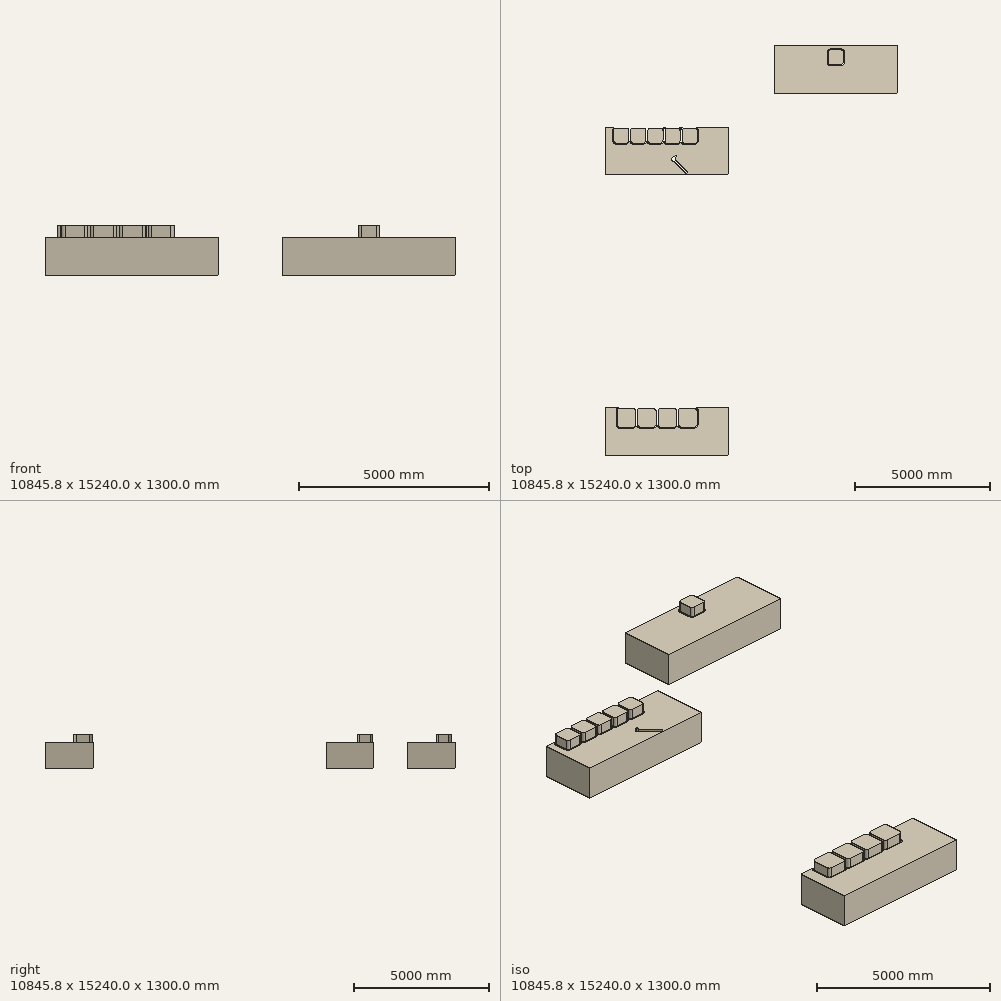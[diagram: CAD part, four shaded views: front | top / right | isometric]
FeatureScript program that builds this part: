
annotation { "Feature Type Name" : "Feature", "Feature Type Description" : "" }
export const myFeature = defineFeature(function(context is Context, id is Id, definition is map)
    precondition{}
    {
        {
            var Q0;
            Q0=qCreatedBy(makeId("Top.planeOp"),FACE);
            var sketch = newSketch(context, id + "F0", { "sketchPlane" : qUnion([Q0])});
            skLineSegment(sketch, "E0", {"start": v(-13462, -12954) * mm, "end": v(13462, -12954) * mm});
            skLineSegment(sketch, "E1", {"start": v(13462, -12954) * mm, "end": v(13462, 12954) * mm});
            skLineSegment(sketch, "E2", {"start": v(13462, 12954) * mm, "end": v(-13462, 12954) * mm});
            skLineSegment(sketch, "E3", {"start": v(-13462, 12954) * mm, "end": v(-13462, -12954) * mm});
            skLineSegment(sketch, "E4", {"start": v(2096.65, -7633.86) * mm, "end": v(3643.75, -7633.86) * mm});
            skLineSegment(sketch, "E5", {"start": v(3643.75, -7633.86) * mm, "end": v(3643.75, -7479.14) * mm});
            skLineSegment(sketch, "E6", {"start": v(3643.75, -7479.14) * mm, "end": v(2096.65, -7479.14) * mm});
            skLineSegment(sketch, "E7", {"start": v(2096.65, -7479.14) * mm, "end": v(2096.65, -7633.86) * mm});
            skLineSegment(sketch, "E8", {"start": v(2096.65, -3188.86) * mm, "end": v(3643.75, -3188.86) * mm});
            skLineSegment(sketch, "E9", {"start": v(3643.75, -3188.86) * mm, "end": v(3643.75, -3034.14) * mm});
            skLineSegment(sketch, "E10", {"start": v(3643.75, -3034.14) * mm, "end": v(2096.65, -3034.14) * mm});
            skLineSegment(sketch, "E11", {"start": v(2096.65, -3034.14) * mm, "end": v(2096.65, -3188.86) * mm});
            skLineSegment(sketch, "E12", {"start": v(2251.36, -7874) * mm, "end": v(3489.04, -7874) * mm});
            skLineSegment(sketch, "E13", {"start": v(3489.04, -7874) * mm, "end": v(3489.04, -2794) * mm});
            skLineSegment(sketch, "E14", {"start": v(3489.04, -2794) * mm, "end": v(2251.36, -2794) * mm});
            skLineSegment(sketch, "E15", {"start": v(2251.36, -2794) * mm, "end": v(2251.36, -7874) * mm});
            skLineSegment(sketch, "E16", {"start": v(2135.33, -7874) * mm, "end": v(2135.33, -2794) * mm});
            skLineSegment(sketch, "E17", {"start": v(2135.33, -2794) * mm, "end": v(2019.3, -2794) * mm});
            skLineSegment(sketch, "E18", {"start": v(2019.3, -2794) * mm, "end": v(2019.3, -7874) * mm});
            skLineSegment(sketch, "E19", {"start": v(2019.3, -7874) * mm, "end": v(2135.33, -7874) * mm});
            skLineSegment(sketch, "E20", {"start": v(3605.07, -7874) * mm, "end": v(3721.1, -7874) * mm});
            skLineSegment(sketch, "E21", {"start": v(3721.1, -7874) * mm, "end": v(3721.1, -2794) * mm});
            skLineSegment(sketch, "E22", {"start": v(3721.1, -2794) * mm, "end": v(3605.07, -2794) * mm});
            skLineSegment(sketch, "E23", {"start": v(3605.07, -2794) * mm, "end": v(3605.07, -7874) * mm});
            skLineSegment(sketch, "E24", {"start": v(-2552.7, -6096) * mm, "end": v(-2552.7, -7874) * mm});
            skLineSegment(sketch, "E25", {"start": v(-2552.7, -7874) * mm, "end": v(2019.3, -7874) * mm});
            skLineSegment(sketch, "E26", {"start": v(2019.3, -7874) * mm, "end": v(2019.3, -6096) * mm});
            skLineSegment(sketch, "E27", {"start": v(2019.3, -6096) * mm, "end": v(-2552.7, -6096) * mm});
            skLineSegment(sketch, "E28", {"start": v(2096.65, -2553.86) * mm, "end": v(3643.75, -2553.86) * mm});
            skLineSegment(sketch, "E29", {"start": v(3643.75, -2553.86) * mm, "end": v(3643.75, -2399.14) * mm});
            skLineSegment(sketch, "E30", {"start": v(3643.75, -2399.14) * mm, "end": v(2096.65, -2399.14) * mm});
            skLineSegment(sketch, "E31", {"start": v(2096.65, -2399.14) * mm, "end": v(2096.65, -2553.86) * mm});
            skLineSegment(sketch, "E32", {"start": v(2096.65, 1891.14) * mm, "end": v(3643.75, 1891.14) * mm});
            skLineSegment(sketch, "E33", {"start": v(3643.75, 1891.14) * mm, "end": v(3643.75, 2045.86) * mm});
            skLineSegment(sketch, "E34", {"start": v(3643.75, 2045.86) * mm, "end": v(2096.65, 2045.86) * mm});
            skLineSegment(sketch, "E35", {"start": v(2096.65, 2045.86) * mm, "end": v(2096.65, 1891.14) * mm});
            skLineSegment(sketch, "E36", {"start": v(2251.36, -2794) * mm, "end": v(3489.04, -2794) * mm});
            skLineSegment(sketch, "E37", {"start": v(3489.04, -2794) * mm, "end": v(3489.04, 2286) * mm});
            skLineSegment(sketch, "E38", {"start": v(3489.04, 2286) * mm, "end": v(2251.36, 2286) * mm});
            skLineSegment(sketch, "E39", {"start": v(2251.36, 2286) * mm, "end": v(2251.36, -2794) * mm});
            skLineSegment(sketch, "E40", {"start": v(2135.33, -2794) * mm, "end": v(2135.33, 2286) * mm});
            skLineSegment(sketch, "E41", {"start": v(2135.33, 2286) * mm, "end": v(2019.3, 2286) * mm});
            skLineSegment(sketch, "E42", {"start": v(2019.3, 2286) * mm, "end": v(2019.3, -2794) * mm});
            skLineSegment(sketch, "E43", {"start": v(2019.3, -2794) * mm, "end": v(2135.33, -2794) * mm});
            skLineSegment(sketch, "E44", {"start": v(3605.07, -2794) * mm, "end": v(3721.1, -2794) * mm});
            skLineSegment(sketch, "E45", {"start": v(3721.1, -2794) * mm, "end": v(3721.1, 2286) * mm});
            skLineSegment(sketch, "E46", {"start": v(3721.1, 2286) * mm, "end": v(3605.07, 2286) * mm});
            skLineSegment(sketch, "E47", {"start": v(3605.07, 2286) * mm, "end": v(3605.07, -2794) * mm});
            skLineSegment(sketch, "E48", {"start": v(-2540, 4335.98) * mm, "end": v(-2540, 2557.98) * mm});
            skLineSegment(sketch, "E49", {"start": v(-2540, 2557.98) * mm, "end": v(2032, 2557.98) * mm});
            skLineSegment(sketch, "E50", {"start": v(2032, 2557.98) * mm, "end": v(2032, 4335.98) * mm});
            skLineSegment(sketch, "E51", {"start": v(2032, 4335.98) * mm, "end": v(-2540, 4335.98) * mm});
            skLineSegment(sketch, "E52", {"start": v(3721.1, 7366) * mm, "end": v(3721.1, 5588) * mm});
            skLineSegment(sketch, "E53", {"start": v(3721.1, 5588) * mm, "end": v(8293.1, 5588) * mm});
            skLineSegment(sketch, "E54", {"start": v(8293.1, 5588) * mm, "end": v(8293.1, 7366) * mm});
            skLineSegment(sketch, "E55", {"start": v(8293.1, 7366) * mm, "end": v(3721.1, 7366) * mm});
            skEllipticalArc(sketch, "E56", {});
            skEllipticalArc(sketch, "E57", {});
            skArc(sketch, "E58", {"start": v(-1177.27, -8073) * mm, "mid": v(-870.7, -8481.42) * mm, "end": v(-400.35, -8680.33) * mm});
            skArc(sketch, "E59", {"start": v(-1227.6, -7904.91) * mm, "mid": v(-1206.2, -7990.08) * mm, "end": v(-1177.27, -8073) * mm});
            skArc(sketch, "E60", {"start": v(-1227.6, -7904.91) * mm, "mid": v(-1242.45, -8002.49) * mm, "end": v(-1247.41, -8101.06) * mm});
            skArc(sketch, "E61", {"start": v(-1247.41, -8101.06) * mm, "mid": v(-266.7, -9081.77) * mm, "end": v(714.01, -8101.06) * mm});
            skArc(sketch, "E62", {"start": v(714.01, -8101.06) * mm, "mid": v(709.05, -8002.49) * mm, "end": v(694.2, -7904.91) * mm});
            skArc(sketch, "E63", {"start": v(643.87, -8073) * mm, "mid": v(672.8, -7990.08) * mm, "end": v(694.2, -7904.91) * mm});
            skArc(sketch, "E64", {"start": v(-186.03, -8686.16) * mm, "mid": v(316.08, -8497.55) * mm, "end": v(643.87, -8073) * mm});
            skEllipticalArc(sketch, "E65", {});
            skEllipticalArc(sketch, "E66", {});
            skEllipticalArc(sketch, "E67", {});
            skArc(sketch, "E68", {"start": v(-1189.97, 2024.77) * mm, "mid": v(-883.4, 1616.35) * mm, "end": v(-413.05, 1417.44) * mm});
            skArc(sketch, "E69", {"start": v(-1240.3, 2192.86) * mm, "mid": v(-1218.9, 2107.69) * mm, "end": v(-1189.97, 2024.77) * mm});
            skArc(sketch, "E70", {"start": v(-1240.3, 2192.86) * mm, "mid": v(-1255.15, 2095.28) * mm, "end": v(-1260.11, 1996.71) * mm});
            skArc(sketch, "E71", {"start": v(-1260.11, 1996.71) * mm, "mid": v(-279.4, 1016) * mm, "end": v(701.31, 1996.71) * mm});
            skArc(sketch, "E72", {"start": v(701.31, 1996.71) * mm, "mid": v(696.35, 2095.28) * mm, "end": v(681.5, 2192.86) * mm});
            skArc(sketch, "E73", {"start": v(631.17, 2024.77) * mm, "mid": v(660.1, 2107.69) * mm, "end": v(681.5, 2192.86) * mm});
            skArc(sketch, "E74", {"start": v(-198.73, 1411.6) * mm, "mid": v(303.38, 1600.22) * mm, "end": v(631.17, 2024.77) * mm});
            skEllipticalArc(sketch, "E75", {});
            skEllipticalArc(sketch, "E76", {});
            skEllipticalArc(sketch, "E77", {});
            skArc(sketch, "E78", {"start": v(5096.53, 5054.8) * mm, "mid": v(5403.1, 4646.37) * mm, "end": v(5873.45, 4447.45) * mm});
            skArc(sketch, "E79", {"start": v(5046.2, 5222.88) * mm, "mid": v(5067.6, 5137.7) * mm, "end": v(5096.53, 5054.8) * mm});
            skArc(sketch, "E80", {"start": v(5046.2, 5222.88) * mm, "mid": v(5031.35, 5125.3) * mm, "end": v(5026.39, 5026.73) * mm});
            skArc(sketch, "E81", {"start": v(5026.39, 5026.73) * mm, "mid": v(6007.1, 4046.02) * mm, "end": v(6987.81, 5026.73) * mm});
            skArc(sketch, "E82", {"start": v(6987.81, 5026.73) * mm, "mid": v(6982.85, 5125.3) * mm, "end": v(6968, 5222.88) * mm});
            skArc(sketch, "E83", {"start": v(6917.67, 5054.8) * mm, "mid": v(6946.6, 5137.7) * mm, "end": v(6968, 5222.88) * mm});
            skArc(sketch, "E84", {"start": v(6087.77, 4441.63) * mm, "mid": v(6589.88, 4630.24) * mm, "end": v(6917.67, 5054.8) * mm});
            skEllipticalArc(sketch, "E85", {});
            skLineSegment(sketch, "E86", {"start": v(-5962.07, -7874) * mm, "end": v(-5962.07, -9906) * mm});
            skLineSegment(sketch, "E87", {"start": v(-5962.07, -9906) * mm, "end": v(-5546.44, -9906) * mm});
            skLineSegment(sketch, "E88", {"start": v(-5546.44, -9906) * mm, "end": v(-5546.44, -7874) * mm});
            skLineSegment(sketch, "E89", {"start": v(-5546.44, -7874) * mm, "end": v(-5962.07, -7874) * mm});
            skLineSegment(sketch, "E90", {"start": v(-5006.1, -9906) * mm, "end": v(-5006.1, -7874) * mm});
            skLineSegment(sketch, "E91", {"start": v(-5006.1, -7874) * mm, "end": v(-4590.47, -7874) * mm});
            skLineSegment(sketch, "E92", {"start": v(-4590.47, -7874) * mm, "end": v(-4590.47, -9906) * mm});
            skLineSegment(sketch, "E93", {"start": v(-4590.47, -9906) * mm, "end": v(-5006.1, -9906) * mm});
            skLineSegment(sketch, "E94", {"start": v(-4064, -7874) * mm, "end": v(-3648.36, -7874) * mm});
            skLineSegment(sketch, "E95", {"start": v(-3648.36, -7874) * mm, "end": v(-3648.36, -9906) * mm});
            skLineSegment(sketch, "E96", {"start": v(-3648.36, -9906) * mm, "end": v(-4064, -9906) * mm});
            skLineSegment(sketch, "E97", {"start": v(-4064, -9906) * mm, "end": v(-4064, -7874) * mm});
            skLineSegment(sketch, "E98", {"start": v(-3302, -8128) * mm, "end": v(-6350, -8128) * mm});
            skLineSegment(sketch, "E99", {"start": v(-6350, -8128) * mm, "end": v(-6350, -8341.36) * mm});
            skLineSegment(sketch, "E100", {"start": v(-6350, -8341.36) * mm, "end": v(-3302, -8341.36) * mm});
            skLineSegment(sketch, "E101", {"start": v(-3302, -8341.36) * mm, "end": v(-3302, -8128) * mm});
            skLineSegment(sketch, "E102", {"start": v(-3302, -8585.2) * mm, "end": v(-6350, -8585.2) * mm});
            skLineSegment(sketch, "E103", {"start": v(-6350, -8585.2) * mm, "end": v(-6350, -8798.56) * mm});
            skLineSegment(sketch, "E104", {"start": v(-6350, -8798.56) * mm, "end": v(-3302, -8798.56) * mm});
            skLineSegment(sketch, "E105", {"start": v(-3302, -8798.56) * mm, "end": v(-3302, -8585.2) * mm});
            skLineSegment(sketch, "E106", {"start": v(-3302, -9042.4) * mm, "end": v(-6350, -9042.4) * mm});
            skLineSegment(sketch, "E107", {"start": v(-6350, -9042.4) * mm, "end": v(-6350, -9255.76) * mm});
            skLineSegment(sketch, "E108", {"start": v(-6350, -9255.76) * mm, "end": v(-3302, -9255.76) * mm});
            skLineSegment(sketch, "E109", {"start": v(-3302, -9255.76) * mm, "end": v(-3302, -9042.4) * mm});
            skLineSegment(sketch, "E110", {"start": v(-3302, -9469.12) * mm, "end": v(-6350, -9469.12) * mm});
            skLineSegment(sketch, "E111", {"start": v(-6350, -9469.12) * mm, "end": v(-6350, -9682.48) * mm});
            skLineSegment(sketch, "E112", {"start": v(-6350, -9682.48) * mm, "end": v(-3302, -9682.48) * mm});
            skLineSegment(sketch, "E113", {"start": v(-3302, -9682.48) * mm, "end": v(-3302, -9469.12) * mm});
            skLineSegment(sketch, "E114", {"start": v(-5962.07, -10240.21) * mm, "end": v(-5962.07, -12272.21) * mm});
            skLineSegment(sketch, "E115", {"start": v(-5962.07, -12272.21) * mm, "end": v(-5546.44, -12272.21) * mm});
            skLineSegment(sketch, "E116", {"start": v(-5546.44, -12272.21) * mm, "end": v(-5546.44, -10240.21) * mm});
            skLineSegment(sketch, "E117", {"start": v(-5546.44, -10240.21) * mm, "end": v(-5962.07, -10240.21) * mm});
            skLineSegment(sketch, "E118", {"start": v(-5006.1, -12272.21) * mm, "end": v(-5006.1, -10240.21) * mm});
            skLineSegment(sketch, "E119", {"start": v(-5006.1, -10240.21) * mm, "end": v(-4590.47, -10240.21) * mm});
            skLineSegment(sketch, "E120", {"start": v(-4590.47, -10240.21) * mm, "end": v(-4590.47, -12272.21) * mm});
            skLineSegment(sketch, "E121", {"start": v(-4590.47, -12272.21) * mm, "end": v(-5006.1, -12272.21) * mm});
            skLineSegment(sketch, "E122", {"start": v(-4064, -10240.21) * mm, "end": v(-3648.36, -10240.21) * mm});
            skLineSegment(sketch, "E123", {"start": v(-3648.36, -10240.21) * mm, "end": v(-3648.36, -12272.21) * mm});
            skLineSegment(sketch, "E124", {"start": v(-3648.36, -12272.21) * mm, "end": v(-4064, -12272.21) * mm});
            skLineSegment(sketch, "E125", {"start": v(-4064, -12272.21) * mm, "end": v(-4064, -10240.21) * mm});
            skLineSegment(sketch, "E126", {"start": v(-3302, -10494.21) * mm, "end": v(-6350, -10494.21) * mm});
            skLineSegment(sketch, "E127", {"start": v(-6350, -10494.21) * mm, "end": v(-6350, -10707.57) * mm});
            skLineSegment(sketch, "E128", {"start": v(-6350, -10707.57) * mm, "end": v(-3302, -10707.57) * mm});
            skLineSegment(sketch, "E129", {"start": v(-3302, -10707.57) * mm, "end": v(-3302, -10494.21) * mm});
            skLineSegment(sketch, "E130", {"start": v(-3302, -10951.41) * mm, "end": v(-6350, -10951.41) * mm});
            skLineSegment(sketch, "E131", {"start": v(-6350, -10951.41) * mm, "end": v(-6350, -11164.77) * mm});
            skLineSegment(sketch, "E132", {"start": v(-6350, -11164.77) * mm, "end": v(-3302, -11164.77) * mm});
            skLineSegment(sketch, "E133", {"start": v(-3302, -11164.77) * mm, "end": v(-3302, -10951.41) * mm});
            skLineSegment(sketch, "E134", {"start": v(-3302, -11408.61) * mm, "end": v(-6350, -11408.61) * mm});
            skLineSegment(sketch, "E135", {"start": v(-6350, -11408.61) * mm, "end": v(-6350, -11621.97) * mm});
            skLineSegment(sketch, "E136", {"start": v(-6350, -11621.97) * mm, "end": v(-3302, -11621.97) * mm});
            skLineSegment(sketch, "E137", {"start": v(-3302, -11621.97) * mm, "end": v(-3302, -11408.61) * mm});
            skLineSegment(sketch, "E138", {"start": v(-3302, -11835.33) * mm, "end": v(-6350, -11835.33) * mm});
            skLineSegment(sketch, "E139", {"start": v(-6350, -11835.33) * mm, "end": v(-6350, -12048.7) * mm});
            skLineSegment(sketch, "E140", {"start": v(-6350, -12048.7) * mm, "end": v(-3302, -12048.7) * mm});
            skLineSegment(sketch, "E141", {"start": v(-3302, -12048.7) * mm, "end": v(-3302, -11835.33) * mm});
            skLineSegment(sketch, "E142", {"start": v(2096.65, 2526.14) * mm, "end": v(3643.75, 2526.14) * mm});
            skLineSegment(sketch, "E143", {"start": v(3643.75, 2526.14) * mm, "end": v(3643.75, 2680.86) * mm});
            skLineSegment(sketch, "E144", {"start": v(3643.75, 2680.86) * mm, "end": v(2096.65, 2680.86) * mm});
            skLineSegment(sketch, "E145", {"start": v(2096.65, 2680.86) * mm, "end": v(2096.65, 2526.14) * mm});
            skLineSegment(sketch, "E146", {"start": v(2096.65, 6971.14) * mm, "end": v(3643.75, 6971.14) * mm});
            skLineSegment(sketch, "E147", {"start": v(3643.75, 6971.14) * mm, "end": v(3643.75, 7125.86) * mm});
            skLineSegment(sketch, "E148", {"start": v(3643.75, 7125.86) * mm, "end": v(2096.65, 7125.86) * mm});
            skLineSegment(sketch, "E149", {"start": v(2096.65, 7125.86) * mm, "end": v(2096.65, 6971.14) * mm});
            skLineSegment(sketch, "E150", {"start": v(2251.36, 2286) * mm, "end": v(3489.04, 2286) * mm});
            skLineSegment(sketch, "E151", {"start": v(3489.04, 2286) * mm, "end": v(3489.04, 7366) * mm});
            skLineSegment(sketch, "E152", {"start": v(3489.04, 7366) * mm, "end": v(2251.36, 7366) * mm});
            skLineSegment(sketch, "E153", {"start": v(2251.36, 7366) * mm, "end": v(2251.36, 2286) * mm});
            skLineSegment(sketch, "E154", {"start": v(2135.33, 2286) * mm, "end": v(2135.33, 7366) * mm});
            skLineSegment(sketch, "E155", {"start": v(2135.33, 7366) * mm, "end": v(2019.3, 7366) * mm});
            skLineSegment(sketch, "E156", {"start": v(2019.3, 7366) * mm, "end": v(2019.3, 2286) * mm});
            skLineSegment(sketch, "E157", {"start": v(2019.3, 2286) * mm, "end": v(2135.33, 2286) * mm});
            skLineSegment(sketch, "E158", {"start": v(3605.07, 2286) * mm, "end": v(3721.1, 2286) * mm});
            skLineSegment(sketch, "E159", {"start": v(3721.1, 2286) * mm, "end": v(3721.1, 7366) * mm});
            skLineSegment(sketch, "E160", {"start": v(3721.1, 7366) * mm, "end": v(3605.07, 7366) * mm});
            skLineSegment(sketch, "E161", {"start": v(3605.07, 7366) * mm, "end": v(3605.07, 2286) * mm});
            skLineSegment(sketch, "E162", {"start": v(-6404.57, 2032) * mm, "end": v(-6404.57, 0) * mm});
            skLineSegment(sketch, "E163", {"start": v(-6404.57, 0) * mm, "end": v(-5988.93, 0) * mm});
            skLineSegment(sketch, "E164", {"start": v(-5988.93, 0) * mm, "end": v(-5988.93, 2032) * mm});
            skLineSegment(sketch, "E165", {"start": v(-5988.93, 2032) * mm, "end": v(-6404.57, 2032) * mm});
            skLineSegment(sketch, "E166", {"start": v(-5448.6, 0) * mm, "end": v(-5448.6, 2032) * mm});
            skLineSegment(sketch, "E167", {"start": v(-5448.6, 2032) * mm, "end": v(-5032.97, 2032) * mm});
            skLineSegment(sketch, "E168", {"start": v(-5032.97, 2032) * mm, "end": v(-5032.97, 0) * mm});
            skLineSegment(sketch, "E169", {"start": v(-5032.97, 0) * mm, "end": v(-5448.6, 0) * mm});
            skLineSegment(sketch, "E170", {"start": v(-4506.5, 2032) * mm, "end": v(-4090.86, 2032) * mm});
            skLineSegment(sketch, "E171", {"start": v(-4090.86, 2032) * mm, "end": v(-4090.86, 0) * mm});
            skLineSegment(sketch, "E172", {"start": v(-4090.86, 0) * mm, "end": v(-4506.5, 0) * mm});
            skLineSegment(sketch, "E173", {"start": v(-4506.5, 0) * mm, "end": v(-4506.5, 2032) * mm});
            skLineSegment(sketch, "E174", {"start": v(-3744.5, 1778) * mm, "end": v(-6792.5, 1778) * mm});
            skLineSegment(sketch, "E175", {"start": v(-6792.5, 1778) * mm, "end": v(-6792.5, 1564.64) * mm});
            skLineSegment(sketch, "E176", {"start": v(-6792.5, 1564.64) * mm, "end": v(-3744.5, 1564.64) * mm});
            skLineSegment(sketch, "E177", {"start": v(-3744.5, 1564.64) * mm, "end": v(-3744.5, 1778) * mm});
            skLineSegment(sketch, "E178", {"start": v(-3744.5, 1320.8) * mm, "end": v(-6792.5, 1320.8) * mm});
            skLineSegment(sketch, "E179", {"start": v(-6792.5, 1320.8) * mm, "end": v(-6792.5, 1107.44) * mm});
            skLineSegment(sketch, "E180", {"start": v(-6792.5, 1107.44) * mm, "end": v(-3744.5, 1107.44) * mm});
            skLineSegment(sketch, "E181", {"start": v(-3744.5, 1107.44) * mm, "end": v(-3744.5, 1320.8) * mm});
            skLineSegment(sketch, "E182", {"start": v(-3744.5, 863.6) * mm, "end": v(-6792.5, 863.6) * mm});
            skLineSegment(sketch, "E183", {"start": v(-6792.5, 863.6) * mm, "end": v(-6792.5, 650.24) * mm});
            skLineSegment(sketch, "E184", {"start": v(-6792.5, 650.24) * mm, "end": v(-3744.5, 650.24) * mm});
            skLineSegment(sketch, "E185", {"start": v(-3744.5, 650.24) * mm, "end": v(-3744.5, 863.6) * mm});
            skLineSegment(sketch, "E186", {"start": v(-3744.5, 436.88) * mm, "end": v(-6792.5, 436.88) * mm});
            skLineSegment(sketch, "E187", {"start": v(-6792.5, 436.88) * mm, "end": v(-6792.5, 223.52) * mm});
            skLineSegment(sketch, "E188", {"start": v(-6792.5, 223.52) * mm, "end": v(-3744.5, 223.52) * mm});
            skLineSegment(sketch, "E189", {"start": v(-3744.5, 223.52) * mm, "end": v(-3744.5, 436.88) * mm});
            skLineSegment(sketch, "E190", {"start": v(-6404.57, -480.26) * mm, "end": v(-6404.57, -2512.26) * mm});
            skLineSegment(sketch, "E191", {"start": v(-6404.57, -2512.26) * mm, "end": v(-5988.93, -2512.26) * mm});
            skLineSegment(sketch, "E192", {"start": v(-5988.93, -2512.26) * mm, "end": v(-5988.93, -480.26) * mm});
            skLineSegment(sketch, "E193", {"start": v(-5988.93, -480.26) * mm, "end": v(-6404.57, -480.26) * mm});
            skLineSegment(sketch, "E194", {"start": v(-5448.6, -2512.26) * mm, "end": v(-5448.6, -480.26) * mm});
            skLineSegment(sketch, "E195", {"start": v(-5448.6, -480.26) * mm, "end": v(-5032.97, -480.26) * mm});
            skLineSegment(sketch, "E196", {"start": v(-5032.97, -480.26) * mm, "end": v(-5032.97, -2512.26) * mm});
            skLineSegment(sketch, "E197", {"start": v(-5032.97, -2512.26) * mm, "end": v(-5448.6, -2512.26) * mm});
            skLineSegment(sketch, "E198", {"start": v(-4506.5, -480.26) * mm, "end": v(-4090.86, -480.26) * mm});
            skLineSegment(sketch, "E199", {"start": v(-4090.86, -480.26) * mm, "end": v(-4090.86, -2512.26) * mm});
            skLineSegment(sketch, "E200", {"start": v(-4090.86, -2512.26) * mm, "end": v(-4506.5, -2512.26) * mm});
            skLineSegment(sketch, "E201", {"start": v(-4506.5, -2512.26) * mm, "end": v(-4506.5, -480.26) * mm});
            skLineSegment(sketch, "E202", {"start": v(-3744.5, -734.26) * mm, "end": v(-6792.5, -734.26) * mm});
            skLineSegment(sketch, "E203", {"start": v(-6792.5, -734.26) * mm, "end": v(-6792.5, -947.62) * mm});
            skLineSegment(sketch, "E204", {"start": v(-6792.5, -947.62) * mm, "end": v(-3744.5, -947.62) * mm});
            skLineSegment(sketch, "E205", {"start": v(-3744.5, -947.62) * mm, "end": v(-3744.5, -734.26) * mm});
            skLineSegment(sketch, "E206", {"start": v(-3744.5, -1191.46) * mm, "end": v(-6792.5, -1191.46) * mm});
            skLineSegment(sketch, "E207", {"start": v(-6792.5, -1191.46) * mm, "end": v(-6792.5, -1404.82) * mm});
            skLineSegment(sketch, "E208", {"start": v(-6792.5, -1404.82) * mm, "end": v(-3744.5, -1404.82) * mm});
            skLineSegment(sketch, "E209", {"start": v(-3744.5, -1404.82) * mm, "end": v(-3744.5, -1191.46) * mm});
            skLineSegment(sketch, "E210", {"start": v(-3744.5, -1648.66) * mm, "end": v(-6792.5, -1648.66) * mm});
            skLineSegment(sketch, "E211", {"start": v(-6792.5, -1648.66) * mm, "end": v(-6792.5, -1862.02) * mm});
            skLineSegment(sketch, "E212", {"start": v(-6792.5, -1862.02) * mm, "end": v(-3744.5, -1862.02) * mm});
            skLineSegment(sketch, "E213", {"start": v(-3744.5, -1862.02) * mm, "end": v(-3744.5, -1648.66) * mm});
            skLineSegment(sketch, "E214", {"start": v(-3744.5, -2075.38) * mm, "end": v(-6792.5, -2075.38) * mm});
            skLineSegment(sketch, "E215", {"start": v(-6792.5, -2075.38) * mm, "end": v(-6792.5, -2288.74) * mm});
            skLineSegment(sketch, "E216", {"start": v(-6792.5, -2288.74) * mm, "end": v(-3744.5, -2288.74) * mm});
            skLineSegment(sketch, "E217", {"start": v(-3744.5, -2288.74) * mm, "end": v(-3744.5, -2075.38) * mm});
            skLineSegment(sketch, "E218", {"start": v(9550.4, 5213.93) * mm, "end": v(11582.4, 5213.93) * mm});
            skLineSegment(sketch, "E219", {"start": v(11582.4, 5213.93) * mm, "end": v(11582.4, 5629.56) * mm});
            skLineSegment(sketch, "E220", {"start": v(11582.4, 5629.56) * mm, "end": v(9550.4, 5629.56) * mm});
            skLineSegment(sketch, "E221", {"start": v(9550.4, 5629.56) * mm, "end": v(9550.4, 5213.93) * mm});
            skLineSegment(sketch, "E222", {"start": v(11582.4, 6169.9) * mm, "end": v(9550.4, 6169.9) * mm});
            skLineSegment(sketch, "E223", {"start": v(9550.4, 6169.9) * mm, "end": v(9550.4, 6585.53) * mm});
            skLineSegment(sketch, "E224", {"start": v(9550.4, 6585.53) * mm, "end": v(11582.4, 6585.53) * mm});
            skLineSegment(sketch, "E225", {"start": v(11582.4, 6585.53) * mm, "end": v(11582.4, 6169.9) * mm});
            skLineSegment(sketch, "E226", {"start": v(9550.4, 7112) * mm, "end": v(9550.4, 7527.64) * mm});
            skLineSegment(sketch, "E227", {"start": v(9550.4, 7527.64) * mm, "end": v(11582.4, 7527.64) * mm});
            skLineSegment(sketch, "E228", {"start": v(11582.4, 7527.64) * mm, "end": v(11582.4, 7112) * mm});
            skLineSegment(sketch, "E229", {"start": v(11582.4, 7112) * mm, "end": v(9550.4, 7112) * mm});
            skLineSegment(sketch, "E230", {"start": v(9804.4, 7874) * mm, "end": v(9804.4, 4826) * mm});
            skLineSegment(sketch, "E231", {"start": v(9804.4, 4826) * mm, "end": v(10017.76, 4826) * mm});
            skLineSegment(sketch, "E232", {"start": v(10017.76, 4826) * mm, "end": v(10017.76, 7874) * mm});
            skLineSegment(sketch, "E233", {"start": v(10017.76, 7874) * mm, "end": v(9804.4, 7874) * mm});
            skLineSegment(sketch, "E234", {"start": v(10261.6, 7874) * mm, "end": v(10261.6, 4826) * mm});
            skLineSegment(sketch, "E235", {"start": v(10261.6, 4826) * mm, "end": v(10474.96, 4826) * mm});
            skLineSegment(sketch, "E236", {"start": v(10474.96, 4826) * mm, "end": v(10474.96, 7874) * mm});
            skLineSegment(sketch, "E237", {"start": v(10474.96, 7874) * mm, "end": v(10261.6, 7874) * mm});
            skLineSegment(sketch, "E238", {"start": v(10718.8, 7874) * mm, "end": v(10718.8, 4826) * mm});
            skLineSegment(sketch, "E239", {"start": v(10718.8, 4826) * mm, "end": v(10932.16, 4826) * mm});
            skLineSegment(sketch, "E240", {"start": v(10932.16, 4826) * mm, "end": v(10932.16, 7874) * mm});
            skLineSegment(sketch, "E241", {"start": v(10932.16, 7874) * mm, "end": v(10718.8, 7874) * mm});
            skLineSegment(sketch, "E242", {"start": v(11145.52, 7874) * mm, "end": v(11145.52, 4826) * mm});
            skLineSegment(sketch, "E243", {"start": v(11145.52, 4826) * mm, "end": v(11358.88, 4826) * mm});
            skLineSegment(sketch, "E244", {"start": v(11358.88, 4826) * mm, "end": v(11358.88, 7874) * mm});
            skLineSegment(sketch, "E245", {"start": v(11358.88, 7874) * mm, "end": v(11145.52, 7874) * mm});
            skLineSegment(sketch, "E246", {"start": v(9789.53, 11494.3) * mm, "end": v(11546.47, 11494.3) * mm});
            skLineSegment(sketch, "E247", {"start": v(11546.47, 11494.3) * mm, "end": v(11546.47, 11897.23) * mm});
            skLineSegment(sketch, "E248", {"start": v(11546.47, 11897.23) * mm, "end": v(11329.73, 11897.23) * mm});
            skEllipticalArc(sketch, "E249", {});
            skLineSegment(sketch, "E250", {"start": v(10765.6, 12031.85) * mm, "end": v(10765.6, 11897.23) * mm});
            skLineSegment(sketch, "E251", {"start": v(10765.6, 11897.23) * mm, "end": v(10570.4, 11897.23) * mm});
            skLineSegment(sketch, "E252", {"start": v(10570.4, 11897.23) * mm, "end": v(10570.4, 12031.85) * mm});
            skEllipticalArc(sketch, "E253", {});
            skLineSegment(sketch, "E254", {"start": v(10006.27, 11897.23) * mm, "end": v(9789.53, 11897.23) * mm});
            skLineSegment(sketch, "E255", {"start": v(9789.53, 11897.23) * mm, "end": v(9789.53, 11494.3) * mm});
            skLineSegment(sketch, "E256", {"start": v(9753.6, 12277.17) * mm, "end": v(10472.11, 11787.89) * mm});
            skLineSegment(sketch, "E257", {"start": v(10472.11, 11787.89) * mm, "end": v(10472.78, 11789.26) * mm});
            skLineSegment(sketch, "E258", {"start": v(10472.78, 11789.26) * mm, "end": v(10472.78, 11551.86) * mm});
            skLineSegment(sketch, "E259", {"start": v(10472.78, 11551.86) * mm, "end": v(10863.22, 11551.86) * mm});
            skLineSegment(sketch, "E260", {"start": v(10863.22, 11551.86) * mm, "end": v(10863.22, 11783.48) * mm});
            skLineSegment(sketch, "E261", {"start": v(10863.22, 11783.48) * mm, "end": v(10863.89, 11782.1) * mm});
            skLineSegment(sketch, "E262", {"start": v(10863.89, 11782.1) * mm, "end": v(11582.4, 12271.39) * mm});
            skLineSegment(sketch, "E263", {"start": v(11582.4, 12271.39) * mm, "end": v(11570.87, 12294.94) * mm});
            skLineSegment(sketch, "E264", {"start": v(11570.87, 12294.94) * mm, "end": v(11570.87, 12386.51) * mm});
            skLineSegment(sketch, "E265", {"start": v(11570.87, 12386.51) * mm, "end": v(10741.2, 12386.51) * mm});
            skLineSegment(sketch, "E266", {"start": v(10741.2, 12386.51) * mm, "end": v(10594.8, 12386.51) * mm});
            skLineSegment(sketch, "E267", {"start": v(10594.8, 12386.51) * mm, "end": v(9765.13, 12386.51) * mm});
            skLineSegment(sketch, "E268", {"start": v(9765.13, 12386.51) * mm, "end": v(9765.13, 12300.72) * mm});
            skLineSegment(sketch, "E269", {"start": v(9765.13, 12300.72) * mm, "end": v(9753.6, 12277.17) * mm});
            skLineSegment(sketch, "E270", {"start": v(10741.2, 11926.01) * mm, "end": v(10741.2, 12271.39) * mm});
            skLineSegment(sketch, "E271", {"start": v(10741.2, 12271.39) * mm, "end": v(11435.99, 12271.39) * mm});
            skLineSegment(sketch, "E272", {"start": v(11435.99, 12271.39) * mm, "end": v(10863.22, 11881.35) * mm});
            skLineSegment(sketch, "E273", {"start": v(10863.22, 11881.35) * mm, "end": v(10863.22, 11926.01) * mm});
            skLineSegment(sketch, "E274", {"start": v(10863.22, 11926.01) * mm, "end": v(10741.2, 11926.01) * mm});
            skLineSegment(sketch, "E275", {"start": v(9908.5, 12271.39) * mm, "end": v(10594.8, 12271.39) * mm});
            skLineSegment(sketch, "E276", {"start": v(10594.8, 12271.39) * mm, "end": v(10594.8, 11926.01) * mm});
            skLineSegment(sketch, "E277", {"start": v(10594.8, 11926.01) * mm, "end": v(10472.78, 11926.01) * mm});
            skLineSegment(sketch, "E278", {"start": v(10472.78, 11926.01) * mm, "end": v(10472.78, 11887.13) * mm});
            skLineSegment(sketch, "E279", {"start": v(10472.78, 11887.13) * mm, "end": v(9908.5, 12271.39) * mm});
            skLineSegment(sketch, "E280", {"start": v(10814.41, 11897.23) * mm, "end": v(10814.41, 11494.3) * mm});
            skLineSegment(sketch, "E281", {"start": v(10814.41, 11494.3) * mm, "end": v(10838.81, 11494.3) * mm});
            skLineSegment(sketch, "E282", {"start": v(10838.81, 11494.3) * mm, "end": v(10838.81, 11897.23) * mm});
            skLineSegment(sketch, "E283", {"start": v(10838.81, 11897.23) * mm, "end": v(10814.41, 11897.23) * mm});
            skLineSegment(sketch, "E284", {"start": v(10521.59, 11897.23) * mm, "end": v(10497.19, 11897.23) * mm});
            skLineSegment(sketch, "E285", {"start": v(10497.19, 11897.23) * mm, "end": v(10497.19, 11494.3) * mm});
            skLineSegment(sketch, "E286", {"start": v(10497.19, 11494.3) * mm, "end": v(10521.59, 11494.3) * mm});
            skLineSegment(sketch, "E287", {"start": v(10521.59, 11494.3) * mm, "end": v(10521.59, 11897.23) * mm});
            skLineSegment(sketch, "E288", {"start": v(9789.53, 10879.42) * mm, "end": v(9789.53, 10735.51) * mm});
            skLineSegment(sketch, "E289", {"start": v(9789.53, 10735.51) * mm, "end": v(11546.47, 10735.51) * mm});
            skLineSegment(sketch, "E290", {"start": v(11546.47, 10735.51) * mm, "end": v(11546.47, 10879.42) * mm});
            skLineSegment(sketch, "E291", {"start": v(11546.47, 10879.42) * mm, "end": v(9789.53, 10879.42) * mm});
            skLineSegment(sketch, "E292", {"start": v(9789.53, 11080.88) * mm, "end": v(9789.53, 10879.42) * mm});
            skLineSegment(sketch, "E293", {"start": v(9789.53, 10879.42) * mm, "end": v(11546.47, 10879.42) * mm});
            skLineSegment(sketch, "E294", {"start": v(11546.47, 10879.42) * mm, "end": v(11546.47, 11080.88) * mm});
            skLineSegment(sketch, "E295", {"start": v(11546.47, 11080.88) * mm, "end": v(9789.53, 11080.88) * mm});
            skLineSegment(sketch, "E296", {"start": v(9789.53, 11397.48) * mm, "end": v(11546.47, 11397.48) * mm});
            skLineSegment(sketch, "E297", {"start": v(11546.47, 11397.48) * mm, "end": v(11546.47, 11483.82) * mm});
            skLineSegment(sketch, "E298", {"start": v(11546.47, 11483.82) * mm, "end": v(9789.53, 11483.82) * mm});
            skLineSegment(sketch, "E299", {"start": v(9789.53, 11483.82) * mm, "end": v(9789.53, 11397.48) * mm});
            skLineSegment(sketch, "E300", {"start": v(9789.53, 11397.48) * mm, "end": v(9789.53, 11080.88) * mm});
            skLineSegment(sketch, "E301", {"start": v(9789.53, 11080.88) * mm, "end": v(11546.47, 11080.88) * mm});
            skLineSegment(sketch, "E302", {"start": v(11546.47, 11080.88) * mm, "end": v(11546.47, 11397.48) * mm});
            skLineSegment(sketch, "E303", {"start": v(11546.47, 11397.48) * mm, "end": v(9789.53, 11397.48) * mm});
            skLineSegment(sketch, "E304", {"start": v(10947.4, 10735.51) * mm, "end": v(10947.4, 7954.21) * mm});
            skLineSegment(sketch, "E305", {"start": v(10947.4, 7954.21) * mm, "end": v(11289.03, 7954.21) * mm});
            skLineSegment(sketch, "E306", {"start": v(11289.03, 7954.21) * mm, "end": v(11289.03, 10735.51) * mm});
            skLineSegment(sketch, "E307", {"start": v(11289.03, 10735.51) * mm, "end": v(10947.4, 10735.51) * mm});
            skLineSegment(sketch, "E308", {"start": v(10014.59, 10735.51) * mm, "end": v(10014.59, 7954.21) * mm});
            skLineSegment(sketch, "E309", {"start": v(10014.59, 7954.21) * mm, "end": v(10356.21, 7954.21) * mm});
            skLineSegment(sketch, "E310", {"start": v(10356.21, 7954.21) * mm, "end": v(10356.21, 10735.51) * mm});
            skLineSegment(sketch, "E311", {"start": v(10356.21, 10735.51) * mm, "end": v(10014.59, 10735.51) * mm});
            skEllipticalArc(sketch, "E312", {});
            skEllipticalArc(sketch, "E313", {});
            skLineSegment(sketch, "E314", {"start": v(-9477.52, -708.09) * mm, "end": v(-9477.52, -2284.43) * mm});
            skLineSegment(sketch, "E315", {"start": v(-10171.2, -1426.61) * mm, "end": v(-10402.43, -1426.61) * mm});
            skLineSegment(sketch, "E316", {"start": v(-10402.43, -1426.61) * mm, "end": v(-10402.43, -765.6) * mm});
            skLineSegment(sketch, "E317", {"start": v(-10402.43, -765.6) * mm, "end": v(-10141.3, -1310.53) * mm});
            skLineSegment(sketch, "E318", {"start": v(-10141.3, -1310.53) * mm, "end": v(-10171.2, -1310.53) * mm});
            skLineSegment(sketch, "E319", {"start": v(-10171.2, -1310.53) * mm, "end": v(-10171.2, -1426.61) * mm});
            skLineSegment(sketch, "E320", {"start": v(-10402.43, -2218.84) * mm, "end": v(-10402.43, -1565.9) * mm});
            skLineSegment(sketch, "E321", {"start": v(-10402.43, -1565.9) * mm, "end": v(-10171.2, -1565.9) * mm});
            skLineSegment(sketch, "E322", {"start": v(-10171.2, -1565.9) * mm, "end": v(-10171.2, -1681.99) * mm});
            skLineSegment(sketch, "E323", {"start": v(-10171.2, -1681.99) * mm, "end": v(-10145.17, -1681.99) * mm});
            skLineSegment(sketch, "E324", {"start": v(-10145.17, -1681.99) * mm, "end": v(-10402.43, -2218.84) * mm});
            skLineSegment(sketch, "E325", {"start": v(-10406.3, -2366.21) * mm, "end": v(-10078.73, -1682.63) * mm});
            skLineSegment(sketch, "E326", {"start": v(-10078.73, -1682.63) * mm, "end": v(-10079.65, -1681.99) * mm});
            skLineSegment(sketch, "E327", {"start": v(-10079.65, -1681.99) * mm, "end": v(-9920.7, -1681.99) * mm});
            skLineSegment(sketch, "E328", {"start": v(-9920.7, -1681.99) * mm, "end": v(-9920.7, -1310.53) * mm});
            skLineSegment(sketch, "E329", {"start": v(-9920.7, -1310.53) * mm, "end": v(-10075.78, -1310.53) * mm});
            skLineSegment(sketch, "E330", {"start": v(-10075.78, -1310.53) * mm, "end": v(-10074.86, -1309.9) * mm});
            skLineSegment(sketch, "E331", {"start": v(-10074.86, -1309.9) * mm, "end": v(-10402.43, -626.31) * mm});
            skLineSegment(sketch, "E332", {"start": v(-10402.43, -626.31) * mm, "end": v(-10418.2, -637.28) * mm});
            skLineSegment(sketch, "E333", {"start": v(-10418.2, -637.28) * mm, "end": v(-10479.5, -637.28) * mm});
            skLineSegment(sketch, "E334", {"start": v(-10479.5, -637.28) * mm, "end": v(-10479.5, -1426.61) * mm});
            skLineSegment(sketch, "E335", {"start": v(-10479.5, -1426.61) * mm, "end": v(-10479.5, -1565.9) * mm});
            skLineSegment(sketch, "E336", {"start": v(-10479.5, -1565.9) * mm, "end": v(-10479.5, -2355.24) * mm});
            skLineSegment(sketch, "E337", {"start": v(-10479.5, -2355.24) * mm, "end": v(-10422.07, -2355.24) * mm});
            skLineSegment(sketch, "E338", {"start": v(-10422.07, -2355.24) * mm, "end": v(-10406.3, -2366.21) * mm});
            skLineSegment(sketch, "E339", {"start": v(-9862.9, -1310.53) * mm, "end": v(-9477.52, -1310.53) * mm});
            skLineSegment(sketch, "E340", {"start": v(-9862.9, -1681.99) * mm, "end": v(-9477.52, -1681.99) * mm});
            skLineSegment(sketch, "E341", {"start": v(-9477.52, -1960.58) * mm, "end": v(-9477.52, -1031.95) * mm});
            skLineSegment(sketch, "E342", {"start": v(-9477.52, -1031.95) * mm, "end": v(-7126.7, -1031.95) * mm});
            skLineSegment(sketch, "E343", {"start": v(-7126.7, -1031.95) * mm, "end": v(-7126.7, -706.93) * mm});
            skLineSegment(sketch, "E344", {"start": v(-7126.7, -706.93) * mm, "end": v(-9477.52, -706.93) * mm});
            skLineSegment(sketch, "E345", {"start": v(-9477.52, -706.93) * mm, "end": v(-9747.28, -706.93) * mm});
            skEllipticalArc(sketch, "E346", {});
            skLineSegment(sketch, "E347", {"start": v(-9747.28, -2285.6) * mm, "end": v(-9477.52, -2285.6) * mm});
            skLineSegment(sketch, "E348", {"start": v(-9477.52, -2285.6) * mm, "end": v(-7126.7, -2285.6) * mm});
            skLineSegment(sketch, "E349", {"start": v(-7126.7, -2285.6) * mm, "end": v(-7126.7, -1960.58) * mm});
            skLineSegment(sketch, "E350", {"start": v(-7126.7, -1960.58) * mm, "end": v(-9477.52, -1960.58) * mm});
            skEllipticalArc(sketch, "E351", {});
            skEllipticalArc(sketch, "E352", {});
            skLineSegment(sketch, "E353", {"start": v(-9035.02, -10468.04) * mm, "end": v(-9035.02, -12044.38) * mm});
            skLineSegment(sketch, "E354", {"start": v(-9728.7, -11186.56) * mm, "end": v(-9959.93, -11186.56) * mm});
            skLineSegment(sketch, "E355", {"start": v(-9959.93, -11186.56) * mm, "end": v(-9959.93, -10525.55) * mm});
            skLineSegment(sketch, "E356", {"start": v(-9959.93, -10525.55) * mm, "end": v(-9698.8, -11070.48) * mm});
            skLineSegment(sketch, "E357", {"start": v(-9698.8, -11070.48) * mm, "end": v(-9728.7, -11070.48) * mm});
            skLineSegment(sketch, "E358", {"start": v(-9728.7, -11070.48) * mm, "end": v(-9728.7, -11186.56) * mm});
            skLineSegment(sketch, "E359", {"start": v(-9959.93, -11978.79) * mm, "end": v(-9959.93, -11325.86) * mm});
            skLineSegment(sketch, "E360", {"start": v(-9959.93, -11325.86) * mm, "end": v(-9728.7, -11325.86) * mm});
            skLineSegment(sketch, "E361", {"start": v(-9728.7, -11325.86) * mm, "end": v(-9728.7, -11441.94) * mm});
            skLineSegment(sketch, "E362", {"start": v(-9728.7, -11441.94) * mm, "end": v(-9702.68, -11441.94) * mm});
            skLineSegment(sketch, "E363", {"start": v(-9702.68, -11441.94) * mm, "end": v(-9959.93, -11978.79) * mm});
            skLineSegment(sketch, "E364", {"start": v(-9963.8, -12126.16) * mm, "end": v(-9636.23, -11442.58) * mm});
            skLineSegment(sketch, "E365", {"start": v(-9636.23, -11442.58) * mm, "end": v(-9637.15, -11441.94) * mm});
            skLineSegment(sketch, "E366", {"start": v(-9637.15, -11441.94) * mm, "end": v(-9478.21, -11441.94) * mm});
            skLineSegment(sketch, "E367", {"start": v(-9478.21, -11441.94) * mm, "end": v(-9478.21, -11070.48) * mm});
            skLineSegment(sketch, "E368", {"start": v(-9478.21, -11070.48) * mm, "end": v(-9633.28, -11070.48) * mm});
            skLineSegment(sketch, "E369", {"start": v(-9633.28, -11070.48) * mm, "end": v(-9632.36, -11069.84) * mm});
            skLineSegment(sketch, "E370", {"start": v(-9632.36, -11069.84) * mm, "end": v(-9959.93, -10386.26) * mm});
            skLineSegment(sketch, "E371", {"start": v(-9959.93, -10386.26) * mm, "end": v(-9975.7, -10397.23) * mm});
            skLineSegment(sketch, "E372", {"start": v(-9975.7, -10397.23) * mm, "end": v(-10037.01, -10397.23) * mm});
            skLineSegment(sketch, "E373", {"start": v(-10037.01, -10397.23) * mm, "end": v(-10037.01, -11186.56) * mm});
            skLineSegment(sketch, "E374", {"start": v(-10037.01, -11186.56) * mm, "end": v(-10037.01, -11325.86) * mm});
            skLineSegment(sketch, "E375", {"start": v(-10037.01, -11325.86) * mm, "end": v(-10037.01, -12115.2) * mm});
            skLineSegment(sketch, "E376", {"start": v(-10037.01, -12115.2) * mm, "end": v(-9979.57, -12115.2) * mm});
            skLineSegment(sketch, "E377", {"start": v(-9979.57, -12115.2) * mm, "end": v(-9963.8, -12126.16) * mm});
            skLineSegment(sketch, "E378", {"start": v(-9420.4, -11070.48) * mm, "end": v(-9035.02, -11070.48) * mm});
            skLineSegment(sketch, "E379", {"start": v(-9420.4, -11441.94) * mm, "end": v(-9035.02, -11441.94) * mm});
            skLineSegment(sketch, "E380", {"start": v(-9035.02, -11720.53) * mm, "end": v(-9035.02, -10791.9) * mm});
            skLineSegment(sketch, "E381", {"start": v(-9035.02, -10791.9) * mm, "end": v(-6684.21, -10791.9) * mm});
            skLineSegment(sketch, "E382", {"start": v(-6684.21, -10791.9) * mm, "end": v(-6684.21, -10466.88) * mm});
            skLineSegment(sketch, "E383", {"start": v(-6684.21, -10466.88) * mm, "end": v(-9035.02, -10466.88) * mm});
            skLineSegment(sketch, "E384", {"start": v(-9035.02, -10466.88) * mm, "end": v(-9304.79, -10466.88) * mm});
            skEllipticalArc(sketch, "E385", {});
            skLineSegment(sketch, "E386", {"start": v(-9304.79, -12045.55) * mm, "end": v(-9035.02, -12045.55) * mm});
            skLineSegment(sketch, "E387", {"start": v(-9035.02, -12045.55) * mm, "end": v(-6684.21, -12045.55) * mm});
            skLineSegment(sketch, "E388", {"start": v(-6684.21, -12045.55) * mm, "end": v(-6684.21, -11720.53) * mm});
            skLineSegment(sketch, "E389", {"start": v(-6684.21, -11720.53) * mm, "end": v(-9035.02, -11720.53) * mm});
            skArc(sketch, "E390", {"start": v(-2032, -6134.1) * mm, "mid": v(-2094.86, -6160.14) * mm, "end": v(-2120.9, -6223) * mm});
            skLineSegment(sketch, "E391", {"start": v(-2120.9, -6223) * mm, "end": v(-2120.9, -6731) * mm});
            skArc(sketch, "E392", {"start": v(-2120.9, -6731) * mm, "mid": v(-2094.86, -6793.86) * mm, "end": v(-2032, -6819.9) * mm});
            skLineSegment(sketch, "E393", {"start": v(-2032, -6819.9) * mm, "end": v(-1524, -6819.9) * mm});
            skArc(sketch, "E394", {"start": v(-1524, -6819.9) * mm, "mid": v(-1461.14, -6793.86) * mm, "end": v(-1435.1, -6731) * mm});
            skLineSegment(sketch, "E395", {"start": v(-1435.1, -6731) * mm, "end": v(-1435.1, -6223) * mm});
            skArc(sketch, "E396", {"start": v(-1435.1, -6223) * mm, "mid": v(-1461.14, -6160.14) * mm, "end": v(-1524, -6134.1) * mm});
            skLineSegment(sketch, "E397", {"start": v(-1524, -6134.1) * mm, "end": v(-2032, -6134.1) * mm});
            skArc(sketch, "E398", {"start": v(-2032, -6096) * mm, "mid": v(-2121.8, -6133.2) * mm, "end": v(-2159, -6223) * mm});
            skLineSegment(sketch, "E399", {"start": v(-2159, -6223) * mm, "end": v(-2159, -6731) * mm});
            skArc(sketch, "E400", {"start": v(-2159, -6731) * mm, "mid": v(-2121.8, -6820.8) * mm, "end": v(-2032, -6858) * mm});
            skLineSegment(sketch, "E401", {"start": v(-2032, -6858) * mm, "end": v(-1524, -6858) * mm});
            skArc(sketch, "E402", {"start": v(-1524, -6858) * mm, "mid": v(-1434.2, -6820.8) * mm, "end": v(-1397, -6731) * mm});
            skLineSegment(sketch, "E403", {"start": v(-1397, -6731) * mm, "end": v(-1397, -6223) * mm});
            skArc(sketch, "E404", {"start": v(-1397, -6223) * mm, "mid": v(-1434.2, -6133.2) * mm, "end": v(-1524, -6096) * mm});
            skLineSegment(sketch, "E405", {"start": v(-1524, -6096) * mm, "end": v(-2032, -6096) * mm});
            skArc(sketch, "E406", {"start": v(-1270, -6134.1) * mm, "mid": v(-1332.86, -6160.14) * mm, "end": v(-1358.9, -6223) * mm});
            skLineSegment(sketch, "E407", {"start": v(-1358.9, -6223) * mm, "end": v(-1358.9, -6731) * mm});
            skArc(sketch, "E408", {"start": v(-1358.9, -6731) * mm, "mid": v(-1332.86, -6793.86) * mm, "end": v(-1270, -6819.9) * mm});
            skLineSegment(sketch, "E409", {"start": v(-1270, -6819.9) * mm, "end": v(-762, -6819.9) * mm});
            skArc(sketch, "E410", {"start": v(-762, -6819.9) * mm, "mid": v(-699.14, -6793.86) * mm, "end": v(-673.1, -6731) * mm});
            skLineSegment(sketch, "E411", {"start": v(-673.1, -6731) * mm, "end": v(-673.1, -6223) * mm});
            skArc(sketch, "E412", {"start": v(-673.1, -6223) * mm, "mid": v(-699.14, -6160.14) * mm, "end": v(-762, -6134.1) * mm});
            skLineSegment(sketch, "E413", {"start": v(-762, -6134.1) * mm, "end": v(-1270, -6134.1) * mm});
            skArc(sketch, "E414", {"start": v(-1270, -6096) * mm, "mid": v(-1359.8, -6133.2) * mm, "end": v(-1397, -6223) * mm});
            skLineSegment(sketch, "E415", {"start": v(-1397, -6223) * mm, "end": v(-1397, -6731) * mm});
            skArc(sketch, "E416", {"start": v(-1397, -6731) * mm, "mid": v(-1359.8, -6820.8) * mm, "end": v(-1270, -6858) * mm});
            skLineSegment(sketch, "E417", {"start": v(-1270, -6858) * mm, "end": v(-762, -6858) * mm});
            skArc(sketch, "E418", {"start": v(-762, -6858) * mm, "mid": v(-672.2, -6820.8) * mm, "end": v(-635, -6731) * mm});
            skLineSegment(sketch, "E419", {"start": v(-635, -6731) * mm, "end": v(-635, -6223) * mm});
            skArc(sketch, "E420", {"start": v(-635, -6223) * mm, "mid": v(-672.2, -6133.2) * mm, "end": v(-762, -6096) * mm});
            skLineSegment(sketch, "E421", {"start": v(-762, -6096) * mm, "end": v(-1270, -6096) * mm});
            skArc(sketch, "E422", {"start": v(-508, -6134.1) * mm, "mid": v(-570.86, -6160.14) * mm, "end": v(-596.9, -6223) * mm});
            skLineSegment(sketch, "E423", {"start": v(-596.9, -6223) * mm, "end": v(-596.9, -6731) * mm});
            skArc(sketch, "E424", {"start": v(-596.9, -6731) * mm, "mid": v(-570.86, -6793.86) * mm, "end": v(-508, -6819.9) * mm});
            skLineSegment(sketch, "E425", {"start": v(-508, -6819.9) * mm, "end": v(0, -6819.9) * mm});
            skArc(sketch, "E426", {"start": v(0, -6819.9) * mm, "mid": v(62.86, -6793.86) * mm, "end": v(88.9, -6731) * mm});
            skLineSegment(sketch, "E427", {"start": v(88.9, -6731) * mm, "end": v(88.9, -6223) * mm});
            skArc(sketch, "E428", {"start": v(88.9, -6223) * mm, "mid": v(62.86, -6160.14) * mm, "end": v(0, -6134.1) * mm});
            skLineSegment(sketch, "E429", {"start": v(0, -6134.1) * mm, "end": v(-508, -6134.1) * mm});
            skArc(sketch, "E430", {"start": v(-508, -6096) * mm, "mid": v(-597.8, -6133.2) * mm, "end": v(-635, -6223) * mm});
            skLineSegment(sketch, "E431", {"start": v(-635, -6223) * mm, "end": v(-635, -6731) * mm});
            skArc(sketch, "E432", {"start": v(-635, -6731) * mm, "mid": v(-597.8, -6820.8) * mm, "end": v(-508, -6858) * mm});
            skLineSegment(sketch, "E433", {"start": v(-508, -6858) * mm, "end": v(0, -6858) * mm});
            skArc(sketch, "E434", {"start": v(0, -6858) * mm, "mid": v(89.8, -6820.8) * mm, "end": v(127, -6731) * mm});
            skLineSegment(sketch, "E435", {"start": v(127, -6731) * mm, "end": v(127, -6223) * mm});
            skArc(sketch, "E436", {"start": v(127, -6223) * mm, "mid": v(89.8, -6133.2) * mm, "end": v(0, -6096) * mm});
            skLineSegment(sketch, "E437", {"start": v(0, -6096) * mm, "end": v(-508, -6096) * mm});
            skArc(sketch, "E438", {"start": v(254, -6134.1) * mm, "mid": v(191.14, -6160.14) * mm, "end": v(165.1, -6223) * mm});
            skLineSegment(sketch, "E439", {"start": v(165.1, -6223) * mm, "end": v(165.1, -6731) * mm});
            skArc(sketch, "E440", {"start": v(165.1, -6731) * mm, "mid": v(191.14, -6793.86) * mm, "end": v(254, -6819.9) * mm});
            skLineSegment(sketch, "E441", {"start": v(254, -6819.9) * mm, "end": v(762, -6819.9) * mm});
            skArc(sketch, "E442", {"start": v(762, -6819.9) * mm, "mid": v(824.86, -6793.86) * mm, "end": v(850.9, -6731) * mm});
            skLineSegment(sketch, "E443", {"start": v(850.9, -6731) * mm, "end": v(850.9, -6223) * mm});
            skArc(sketch, "E444", {"start": v(850.9, -6223) * mm, "mid": v(824.86, -6160.14) * mm, "end": v(762, -6134.1) * mm});
            skLineSegment(sketch, "E445", {"start": v(762, -6134.1) * mm, "end": v(254, -6134.1) * mm});
            skArc(sketch, "E446", {"start": v(254, -6096) * mm, "mid": v(164.2, -6133.2) * mm, "end": v(127, -6223) * mm});
            skLineSegment(sketch, "E447", {"start": v(127, -6223) * mm, "end": v(127, -6731) * mm});
            skArc(sketch, "E448", {"start": v(127, -6731) * mm, "mid": v(164.2, -6820.8) * mm, "end": v(254, -6858) * mm});
            skLineSegment(sketch, "E449", {"start": v(254, -6858) * mm, "end": v(762, -6858) * mm});
            skArc(sketch, "E450", {"start": v(762, -6858) * mm, "mid": v(851.8, -6820.8) * mm, "end": v(889, -6731) * mm});
            skLineSegment(sketch, "E451", {"start": v(889, -6731) * mm, "end": v(889, -6223) * mm});
            skArc(sketch, "E452", {"start": v(889, -6223) * mm, "mid": v(851.8, -6133.2) * mm, "end": v(762, -6096) * mm});
            skLineSegment(sketch, "E453", {"start": v(762, -6096) * mm, "end": v(254, -6096) * mm});
            skArc(sketch, "E454", {"start": v(-2159, 4297.88) * mm, "mid": v(-2221.86, 4271.84) * mm, "end": v(-2247.9, 4208.98) * mm});
            skLineSegment(sketch, "E455", {"start": v(-2247.9, 4208.98) * mm, "end": v(-2247.9, 3827.98) * mm});
            skArc(sketch, "E456", {"start": v(-2247.9, 3827.98) * mm, "mid": v(-2221.86, 3765.12) * mm, "end": v(-2159, 3739.08) * mm});
            skLineSegment(sketch, "E457", {"start": v(-2159, 3739.08) * mm, "end": v(-1778, 3739.08) * mm});
            skArc(sketch, "E458", {"start": v(-1778, 3739.08) * mm, "mid": v(-1715.14, 3765.12) * mm, "end": v(-1689.1, 3827.98) * mm});
            skLineSegment(sketch, "E459", {"start": v(-1689.1, 3827.98) * mm, "end": v(-1689.1, 4208.98) * mm});
            skArc(sketch, "E460", {"start": v(-1689.1, 4208.98) * mm, "mid": v(-1715.14, 4271.84) * mm, "end": v(-1778, 4297.88) * mm});
            skLineSegment(sketch, "E461", {"start": v(-1778, 4297.88) * mm, "end": v(-2159, 4297.88) * mm});
            skArc(sketch, "E462", {"start": v(-2159, 4335.98) * mm, "mid": v(-2248.8, 4298.78) * mm, "end": v(-2286, 4208.98) * mm});
            skLineSegment(sketch, "E463", {"start": v(-2286, 4208.98) * mm, "end": v(-2286, 3827.98) * mm});
            skArc(sketch, "E464", {"start": v(-2286, 3827.98) * mm, "mid": v(-2248.8, 3738.18) * mm, "end": v(-2159, 3700.98) * mm});
            skLineSegment(sketch, "E465", {"start": v(-2159, 3700.98) * mm, "end": v(-1778, 3700.98) * mm});
            skArc(sketch, "E466", {"start": v(-1778, 3700.98) * mm, "mid": v(-1688.2, 3738.18) * mm, "end": v(-1651, 3827.98) * mm});
            skLineSegment(sketch, "E467", {"start": v(-1651, 3827.98) * mm, "end": v(-1651, 4208.98) * mm});
            skArc(sketch, "E468", {"start": v(-1651, 4208.98) * mm, "mid": v(-1688.2, 4298.78) * mm, "end": v(-1778, 4335.98) * mm});
            skLineSegment(sketch, "E469", {"start": v(-1778, 4335.98) * mm, "end": v(-2159, 4335.98) * mm});
            skArc(sketch, "E470", {"start": v(-1524, 4297.88) * mm, "mid": v(-1586.86, 4271.84) * mm, "end": v(-1612.9, 4208.98) * mm});
            skLineSegment(sketch, "E471", {"start": v(-1612.9, 4208.98) * mm, "end": v(-1612.9, 3827.98) * mm});
            skArc(sketch, "E472", {"start": v(-1612.9, 3827.98) * mm, "mid": v(-1586.86, 3765.12) * mm, "end": v(-1524, 3739.08) * mm});
            skLineSegment(sketch, "E473", {"start": v(-1524, 3739.08) * mm, "end": v(-1143, 3739.08) * mm});
            skArc(sketch, "E474", {"start": v(-1143, 3739.08) * mm, "mid": v(-1080.14, 3765.12) * mm, "end": v(-1054.1, 3827.98) * mm});
            skLineSegment(sketch, "E475", {"start": v(-1054.1, 3827.98) * mm, "end": v(-1054.1, 4208.98) * mm});
            skArc(sketch, "E476", {"start": v(-1054.1, 4208.98) * mm, "mid": v(-1080.14, 4271.84) * mm, "end": v(-1143, 4297.88) * mm});
            skLineSegment(sketch, "E477", {"start": v(-1143, 4297.88) * mm, "end": v(-1524, 4297.88) * mm});
            skArc(sketch, "E478", {"start": v(-1524, 4335.98) * mm, "mid": v(-1613.8, 4298.78) * mm, "end": v(-1651, 4208.98) * mm});
            skLineSegment(sketch, "E479", {"start": v(-1651, 4208.98) * mm, "end": v(-1651, 3827.98) * mm});
            skArc(sketch, "E480", {"start": v(-1651, 3827.98) * mm, "mid": v(-1613.8, 3738.18) * mm, "end": v(-1524, 3700.98) * mm});
            skLineSegment(sketch, "E481", {"start": v(-1524, 3700.98) * mm, "end": v(-1143, 3700.98) * mm});
            skArc(sketch, "E482", {"start": v(-1143, 3700.98) * mm, "mid": v(-1053.2, 3738.18) * mm, "end": v(-1016, 3827.98) * mm});
            skLineSegment(sketch, "E483", {"start": v(-1016, 3827.98) * mm, "end": v(-1016, 4208.98) * mm});
            skArc(sketch, "E484", {"start": v(-1016, 4208.98) * mm, "mid": v(-1053.2, 4298.78) * mm, "end": v(-1143, 4335.98) * mm});
            skLineSegment(sketch, "E485", {"start": v(-1143, 4335.98) * mm, "end": v(-1524, 4335.98) * mm});
            skArc(sketch, "E486", {"start": v(-889, 4297.88) * mm, "mid": v(-951.86, 4271.84) * mm, "end": v(-977.9, 4208.98) * mm});
            skLineSegment(sketch, "E487", {"start": v(-977.9, 4208.98) * mm, "end": v(-977.9, 3827.98) * mm});
            skArc(sketch, "E488", {"start": v(-977.9, 3827.98) * mm, "mid": v(-951.86, 3765.12) * mm, "end": v(-889, 3739.08) * mm});
            skLineSegment(sketch, "E489", {"start": v(-889, 3739.08) * mm, "end": v(-508, 3739.08) * mm});
            skArc(sketch, "E490", {"start": v(-508, 3739.08) * mm, "mid": v(-445.14, 3765.12) * mm, "end": v(-419.1, 3827.98) * mm});
            skLineSegment(sketch, "E491", {"start": v(-419.1, 3827.98) * mm, "end": v(-419.1, 4208.98) * mm});
            skArc(sketch, "E492", {"start": v(-419.1, 4208.98) * mm, "mid": v(-445.14, 4271.84) * mm, "end": v(-508, 4297.88) * mm});
            skLineSegment(sketch, "E493", {"start": v(-508, 4297.88) * mm, "end": v(-889, 4297.88) * mm});
            skArc(sketch, "E494", {"start": v(-889, 4335.98) * mm, "mid": v(-978.8, 4298.78) * mm, "end": v(-1016, 4208.98) * mm});
            skLineSegment(sketch, "E495", {"start": v(-1016, 4208.98) * mm, "end": v(-1016, 3827.98) * mm});
            skArc(sketch, "E496", {"start": v(-1016, 3827.98) * mm, "mid": v(-978.8, 3738.18) * mm, "end": v(-889, 3700.98) * mm});
            skLineSegment(sketch, "E497", {"start": v(-889, 3700.98) * mm, "end": v(-508, 3700.98) * mm});
            skArc(sketch, "E498", {"start": v(-508, 3700.98) * mm, "mid": v(-418.2, 3738.18) * mm, "end": v(-381, 3827.98) * mm});
            skLineSegment(sketch, "E499", {"start": v(-381, 3827.98) * mm, "end": v(-381, 4208.98) * mm});
            skArc(sketch, "E500", {"start": v(-381, 4208.98) * mm, "mid": v(-418.2, 4298.78) * mm, "end": v(-508, 4335.98) * mm});
            skLineSegment(sketch, "E501", {"start": v(-508, 4335.98) * mm, "end": v(-889, 4335.98) * mm});
            skArc(sketch, "E502", {"start": v(-254, 4281.17) * mm, "mid": v(-316.86, 4255.13) * mm, "end": v(-342.9, 4192.27) * mm});
            skLineSegment(sketch, "E503", {"start": v(-342.9, 4192.27) * mm, "end": v(-342.9, 3811.27) * mm});
            skArc(sketch, "E504", {"start": v(-342.9, 3811.27) * mm, "mid": v(-316.86, 3748.4) * mm, "end": v(-254, 3722.37) * mm});
            skLineSegment(sketch, "E505", {"start": v(-254, 3722.37) * mm, "end": v(127, 3722.37) * mm});
            skArc(sketch, "E506", {"start": v(127, 3722.37) * mm, "mid": v(189.86, 3748.4) * mm, "end": v(215.9, 3811.27) * mm});
            skLineSegment(sketch, "E507", {"start": v(215.9, 3811.27) * mm, "end": v(215.9, 4192.27) * mm});
            skArc(sketch, "E508", {"start": v(215.9, 4192.27) * mm, "mid": v(189.86, 4255.13) * mm, "end": v(127, 4281.17) * mm});
            skLineSegment(sketch, "E509", {"start": v(127, 4281.17) * mm, "end": v(-254, 4281.17) * mm});
            skArc(sketch, "E510", {"start": v(-254, 4319.27) * mm, "mid": v(-343.8, 4282.07) * mm, "end": v(-381, 4192.27) * mm});
            skLineSegment(sketch, "E511", {"start": v(-381, 4192.27) * mm, "end": v(-381, 3811.27) * mm});
            skArc(sketch, "E512", {"start": v(-381, 3811.27) * mm, "mid": v(-343.8, 3721.47) * mm, "end": v(-254, 3684.27) * mm});
            skLineSegment(sketch, "E513", {"start": v(-254, 3684.27) * mm, "end": v(127, 3684.27) * mm});
            skArc(sketch, "E514", {"start": v(127, 3684.27) * mm, "mid": v(216.8, 3721.47) * mm, "end": v(254, 3811.27) * mm});
            skLineSegment(sketch, "E515", {"start": v(254, 3811.27) * mm, "end": v(254, 4192.27) * mm});
            skArc(sketch, "E516", {"start": v(254, 4192.27) * mm, "mid": v(216.8, 4282.07) * mm, "end": v(127, 4319.27) * mm});
            skLineSegment(sketch, "E517", {"start": v(127, 4319.27) * mm, "end": v(-254, 4319.27) * mm});
            skArc(sketch, "E518", {"start": v(381, 4281.17) * mm, "mid": v(318.14, 4255.13) * mm, "end": v(292.1, 4192.27) * mm});
            skLineSegment(sketch, "E519", {"start": v(292.1, 4192.27) * mm, "end": v(292.1, 3811.27) * mm});
            skArc(sketch, "E520", {"start": v(292.1, 3811.27) * mm, "mid": v(318.14, 3748.4) * mm, "end": v(381, 3722.37) * mm});
            skLineSegment(sketch, "E521", {"start": v(381, 3722.37) * mm, "end": v(762, 3722.37) * mm});
            skArc(sketch, "E522", {"start": v(762, 3722.37) * mm, "mid": v(824.86, 3748.4) * mm, "end": v(850.9, 3811.27) * mm});
            skLineSegment(sketch, "E523", {"start": v(850.9, 3811.27) * mm, "end": v(850.9, 4192.27) * mm});
            skArc(sketch, "E524", {"start": v(850.9, 4192.27) * mm, "mid": v(824.86, 4255.13) * mm, "end": v(762, 4281.17) * mm});
            skLineSegment(sketch, "E525", {"start": v(762, 4281.17) * mm, "end": v(381, 4281.17) * mm});
            skArc(sketch, "E526", {"start": v(381, 4319.27) * mm, "mid": v(291.2, 4282.07) * mm, "end": v(254, 4192.27) * mm});
            skLineSegment(sketch, "E527", {"start": v(254, 4192.27) * mm, "end": v(254, 3811.27) * mm});
            skArc(sketch, "E528", {"start": v(254, 3811.27) * mm, "mid": v(291.2, 3721.47) * mm, "end": v(381, 3684.27) * mm});
            skLineSegment(sketch, "E529", {"start": v(381, 3684.27) * mm, "end": v(762, 3684.27) * mm});
            skArc(sketch, "E530", {"start": v(762, 3684.27) * mm, "mid": v(851.8, 3721.47) * mm, "end": v(889, 3811.27) * mm});
            skLineSegment(sketch, "E531", {"start": v(889, 3811.27) * mm, "end": v(889, 4192.27) * mm});
            skArc(sketch, "E532", {"start": v(889, 4192.27) * mm, "mid": v(851.8, 4282.07) * mm, "end": v(762, 4319.27) * mm});
            skLineSegment(sketch, "E533", {"start": v(762, 4319.27) * mm, "end": v(381, 4319.27) * mm});
            skArc(sketch, "E534", {"start": v(5816.6, 7200.9) * mm, "mid": v(5753.74, 7174.86) * mm, "end": v(5727.7, 7112) * mm});
            skLineSegment(sketch, "E535", {"start": v(5727.7, 7112) * mm, "end": v(5727.7, 6731) * mm});
            skArc(sketch, "E536", {"start": v(5727.7, 6731) * mm, "mid": v(5753.74, 6668.14) * mm, "end": v(5816.6, 6642.1) * mm});
            skLineSegment(sketch, "E537", {"start": v(5816.6, 6642.1) * mm, "end": v(6197.6, 6642.1) * mm});
            skArc(sketch, "E538", {"start": v(6197.6, 6642.1) * mm, "mid": v(6260.46, 6668.14) * mm, "end": v(6286.5, 6731) * mm});
            skLineSegment(sketch, "E539", {"start": v(6286.5, 6731) * mm, "end": v(6286.5, 7112) * mm});
            skArc(sketch, "E540", {"start": v(6286.5, 7112) * mm, "mid": v(6260.46, 7174.86) * mm, "end": v(6197.6, 7200.9) * mm});
            skLineSegment(sketch, "E541", {"start": v(6197.6, 7200.9) * mm, "end": v(5816.6, 7200.9) * mm});
            skArc(sketch, "E542", {"start": v(5816.6, 7239) * mm, "mid": v(5726.8, 7201.8) * mm, "end": v(5689.6, 7112) * mm});
            skLineSegment(sketch, "E543", {"start": v(5689.6, 7112) * mm, "end": v(5689.6, 6731) * mm});
            skArc(sketch, "E544", {"start": v(5689.6, 6731) * mm, "mid": v(5726.8, 6641.2) * mm, "end": v(5816.6, 6604) * mm});
            skLineSegment(sketch, "E545", {"start": v(5816.6, 6604) * mm, "end": v(6197.6, 6604) * mm});
            skArc(sketch, "E546", {"start": v(6197.6, 6604) * mm, "mid": v(6287.4, 6641.2) * mm, "end": v(6324.6, 6731) * mm});
            skLineSegment(sketch, "E547", {"start": v(6324.6, 6731) * mm, "end": v(6324.6, 7112) * mm});
            skArc(sketch, "E548", {"start": v(6324.6, 7112) * mm, "mid": v(6287.4, 7201.8) * mm, "end": v(6197.6, 7239) * mm});
            skLineSegment(sketch, "E549", {"start": v(6197.6, 7239) * mm, "end": v(5816.6, 7239) * mm});
            skArc(sketch, "E550", {"start": v(-5270.5, -8356.6) * mm, "mid": v(-5333.36, -8382.64) * mm, "end": v(-5359.4, -8445.5) * mm});
            skLineSegment(sketch, "E551", {"start": v(-5359.4, -8445.5) * mm, "end": v(-5359.4, -9334.5) * mm});
            skArc(sketch, "E552", {"start": v(-5359.4, -9334.5) * mm, "mid": v(-5333.36, -9397.36) * mm, "end": v(-5270.5, -9423.4) * mm});
            skLineSegment(sketch, "E553", {"start": v(-5270.5, -9423.4) * mm, "end": v(-4381.5, -9423.4) * mm});
            skArc(sketch, "E554", {"start": v(-4381.5, -9423.4) * mm, "mid": v(-4318.64, -9397.36) * mm, "end": v(-4292.6, -9334.5) * mm});
            skLineSegment(sketch, "E555", {"start": v(-4292.6, -9334.5) * mm, "end": v(-4292.6, -8445.5) * mm});
            skArc(sketch, "E556", {"start": v(-4292.6, -8445.5) * mm, "mid": v(-4318.64, -8382.64) * mm, "end": v(-4381.5, -8356.6) * mm});
            skLineSegment(sketch, "E557", {"start": v(-4381.5, -8356.6) * mm, "end": v(-5270.5, -8356.6) * mm});
            skArc(sketch, "E558", {"start": v(-5270.5, -8318.5) * mm, "mid": v(-5360.3, -8355.7) * mm, "end": v(-5397.5, -8445.5) * mm});
            skLineSegment(sketch, "E559", {"start": v(-5397.5, -8445.5) * mm, "end": v(-5397.5, -9334.5) * mm});
            skArc(sketch, "E560", {"start": v(-5397.5, -9334.5) * mm, "mid": v(-5360.3, -9424.3) * mm, "end": v(-5270.5, -9461.5) * mm});
            skLineSegment(sketch, "E561", {"start": v(-5270.5, -9461.5) * mm, "end": v(-4381.5, -9461.5) * mm});
            skArc(sketch, "E562", {"start": v(-4381.5, -9461.5) * mm, "mid": v(-4291.7, -9424.3) * mm, "end": v(-4254.5, -9334.5) * mm});
            skLineSegment(sketch, "E563", {"start": v(-4254.5, -9334.5) * mm, "end": v(-4254.5, -8445.5) * mm});
            skArc(sketch, "E564", {"start": v(-4254.5, -8445.5) * mm, "mid": v(-4291.7, -8355.7) * mm, "end": v(-4381.5, -8318.5) * mm});
            skLineSegment(sketch, "E565", {"start": v(-4381.5, -8318.5) * mm, "end": v(-5270.5, -8318.5) * mm});
            skArc(sketch, "E566", {"start": v(-5842, -10424.36) * mm, "mid": v(-5904.86, -10450.4) * mm, "end": v(-5930.9, -10513.26) * mm});
            skLineSegment(sketch, "E567", {"start": v(-5930.9, -10513.26) * mm, "end": v(-5930.9, -11021.26) * mm});
            skArc(sketch, "E568", {"start": v(-5930.9, -11021.26) * mm, "mid": v(-5904.86, -11084.12) * mm, "end": v(-5842, -11110.16) * mm});
            skLineSegment(sketch, "E569", {"start": v(-5842, -11110.16) * mm, "end": v(-5156.2, -11110.16) * mm});
            skArc(sketch, "E570", {"start": v(-5156.2, -11110.16) * mm, "mid": v(-5093.34, -11084.12) * mm, "end": v(-5067.3, -11021.26) * mm});
            skLineSegment(sketch, "E571", {"start": v(-5067.3, -11021.26) * mm, "end": v(-5067.3, -10513.26) * mm});
            skArc(sketch, "E572", {"start": v(-5067.3, -10513.26) * mm, "mid": v(-5093.34, -10450.4) * mm, "end": v(-5156.2, -10424.36) * mm});
            skLineSegment(sketch, "E573", {"start": v(-5156.2, -10424.36) * mm, "end": v(-5842, -10424.36) * mm});
            skArc(sketch, "E574", {"start": v(-5842, -10386.26) * mm, "mid": v(-5931.8, -10423.46) * mm, "end": v(-5969, -10513.26) * mm});
            skLineSegment(sketch, "E575", {"start": v(-5969, -10513.26) * mm, "end": v(-5969, -11021.26) * mm});
            skArc(sketch, "E576", {"start": v(-5969, -11021.26) * mm, "mid": v(-5931.8, -11111.06) * mm, "end": v(-5842, -11148.26) * mm});
            skLineSegment(sketch, "E577", {"start": v(-5842, -11148.26) * mm, "end": v(-5156.2, -11148.26) * mm});
            skArc(sketch, "E578", {"start": v(-5156.2, -11148.26) * mm, "mid": v(-5066.4, -11111.06) * mm, "end": v(-5029.2, -11021.26) * mm});
            skLineSegment(sketch, "E579", {"start": v(-5029.2, -11021.26) * mm, "end": v(-5029.2, -10513.26) * mm});
            skArc(sketch, "E580", {"start": v(-5029.2, -10513.26) * mm, "mid": v(-5066.4, -10423.46) * mm, "end": v(-5156.2, -10386.26) * mm});
            skLineSegment(sketch, "E581", {"start": v(-5156.2, -10386.26) * mm, "end": v(-5842, -10386.26) * mm});
            skArc(sketch, "E582", {"start": v(-4699, -10415.38) * mm, "mid": v(-4761.86, -10441.42) * mm, "end": v(-4787.9, -10504.28) * mm});
            skLineSegment(sketch, "E583", {"start": v(-4787.9, -10504.28) * mm, "end": v(-4787.9, -11062.84) * mm});
            skArc(sketch, "E584", {"start": v(-4787.9, -11062.84) * mm, "mid": v(-4761.86, -11125.7) * mm, "end": v(-4699, -11151.74) * mm});
            skLineSegment(sketch, "E585", {"start": v(-4699, -11151.74) * mm, "end": v(-3810, -11151.74) * mm});
            skArc(sketch, "E586", {"start": v(-3810, -11151.74) * mm, "mid": v(-3747.14, -11125.7) * mm, "end": v(-3721.1, -11062.84) * mm});
            skLineSegment(sketch, "E587", {"start": v(-3721.1, -11062.84) * mm, "end": v(-3721.1, -10504.28) * mm});
            skArc(sketch, "E588", {"start": v(-3721.1, -10504.28) * mm, "mid": v(-3747.14, -10441.42) * mm, "end": v(-3810, -10415.38) * mm});
            skLineSegment(sketch, "E589", {"start": v(-3810, -10415.38) * mm, "end": v(-4699, -10415.38) * mm});
            skArc(sketch, "E590", {"start": v(-4699, -10377.28) * mm, "mid": v(-4788.8, -10414.48) * mm, "end": v(-4826, -10504.28) * mm});
            skLineSegment(sketch, "E591", {"start": v(-4826, -10504.28) * mm, "end": v(-4826, -11062.84) * mm});
            skArc(sketch, "E592", {"start": v(-4826, -11062.84) * mm, "mid": v(-4788.8, -11152.65) * mm, "end": v(-4699, -11189.84) * mm});
            skLineSegment(sketch, "E593", {"start": v(-4699, -11189.84) * mm, "end": v(-3810, -11189.84) * mm});
            skArc(sketch, "E594", {"start": v(-3810, -11189.84) * mm, "mid": v(-3720.2, -11152.65) * mm, "end": v(-3683, -11062.84) * mm});
            skLineSegment(sketch, "E595", {"start": v(-3683, -11062.84) * mm, "end": v(-3683, -10504.28) * mm});
            skArc(sketch, "E596", {"start": v(-3683, -10504.28) * mm, "mid": v(-3720.2, -10414.48) * mm, "end": v(-3810, -10377.28) * mm});
            skLineSegment(sketch, "E597", {"start": v(-3810, -10377.28) * mm, "end": v(-4699, -10377.28) * mm});
            skArc(sketch, "E598", {"start": v(-5842, -11402.26) * mm, "mid": v(-5904.86, -11428.3) * mm, "end": v(-5930.9, -11491.16) * mm});
            skLineSegment(sketch, "E599", {"start": v(-5930.9, -11491.16) * mm, "end": v(-5930.9, -11999.16) * mm});
            skArc(sketch, "E600", {"start": v(-5930.9, -11999.16) * mm, "mid": v(-5904.86, -12062.02) * mm, "end": v(-5842, -12088.06) * mm});
            skLineSegment(sketch, "E601", {"start": v(-5842, -12088.06) * mm, "end": v(-5080, -12088.06) * mm});
            skArc(sketch, "E602", {"start": v(-5080, -12088.06) * mm, "mid": v(-5017.14, -12062.02) * mm, "end": v(-4991.1, -11999.16) * mm});
            skLineSegment(sketch, "E603", {"start": v(-4991.1, -11999.16) * mm, "end": v(-4991.1, -11491.16) * mm});
            skArc(sketch, "E604", {"start": v(-4991.1, -11491.16) * mm, "mid": v(-5017.14, -11428.3) * mm, "end": v(-5080, -11402.26) * mm});
            skLineSegment(sketch, "E605", {"start": v(-5080, -11402.26) * mm, "end": v(-5842, -11402.26) * mm});
            skArc(sketch, "E606", {"start": v(-5842, -11364.16) * mm, "mid": v(-5931.8, -11401.36) * mm, "end": v(-5969, -11491.16) * mm});
            skLineSegment(sketch, "E607", {"start": v(-5969, -11491.16) * mm, "end": v(-5969, -11999.16) * mm});
            skArc(sketch, "E608", {"start": v(-5969, -11999.16) * mm, "mid": v(-5931.8, -12088.96) * mm, "end": v(-5842, -12126.16) * mm});
            skLineSegment(sketch, "E609", {"start": v(-5842, -12126.16) * mm, "end": v(-5080, -12126.16) * mm});
            skArc(sketch, "E610", {"start": v(-5080, -12126.16) * mm, "mid": v(-4990.2, -12088.96) * mm, "end": v(-4953, -11999.16) * mm});
            skLineSegment(sketch, "E611", {"start": v(-4953, -11999.16) * mm, "end": v(-4953, -11491.16) * mm});
            skArc(sketch, "E612", {"start": v(-4953, -11491.16) * mm, "mid": v(-4990.2, -11401.36) * mm, "end": v(-5080, -11364.16) * mm});
            skLineSegment(sketch, "E613", {"start": v(-5080, -11364.16) * mm, "end": v(-5842, -11364.16) * mm});
            skArc(sketch, "E614", {"start": v(-4699, -11402.26) * mm, "mid": v(-4761.86, -11428.3) * mm, "end": v(-4787.9, -11491.16) * mm});
            skLineSegment(sketch, "E615", {"start": v(-4787.9, -11491.16) * mm, "end": v(-4787.9, -11999.16) * mm});
            skArc(sketch, "E616", {"start": v(-4787.9, -11999.16) * mm, "mid": v(-4761.86, -12062.02) * mm, "end": v(-4699, -12088.06) * mm});
            skLineSegment(sketch, "E617", {"start": v(-4699, -12088.06) * mm, "end": v(-3810, -12088.06) * mm});
            skArc(sketch, "E618", {"start": v(-3810, -12088.06) * mm, "mid": v(-3747.14, -12062.02) * mm, "end": v(-3721.1, -11999.16) * mm});
            skLineSegment(sketch, "E619", {"start": v(-3721.1, -11999.16) * mm, "end": v(-3721.1, -11491.16) * mm});
            skArc(sketch, "E620", {"start": v(-3721.1, -11491.16) * mm, "mid": v(-3747.14, -11428.3) * mm, "end": v(-3810, -11402.26) * mm});
            skLineSegment(sketch, "E621", {"start": v(-3810, -11402.26) * mm, "end": v(-4699, -11402.26) * mm});
            skArc(sketch, "E622", {"start": v(-4699, -11364.16) * mm, "mid": v(-4788.8, -11401.36) * mm, "end": v(-4826, -11491.16) * mm});
            skLineSegment(sketch, "E623", {"start": v(-4826, -11491.16) * mm, "end": v(-4826, -11999.16) * mm});
            skArc(sketch, "E624", {"start": v(-4826, -11999.16) * mm, "mid": v(-4788.8, -12088.96) * mm, "end": v(-4699, -12126.16) * mm});
            skLineSegment(sketch, "E625", {"start": v(-4699, -12126.16) * mm, "end": v(-3810, -12126.16) * mm});
            skArc(sketch, "E626", {"start": v(-3810, -12126.16) * mm, "mid": v(-3720.2, -12088.96) * mm, "end": v(-3683, -11999.16) * mm});
            skLineSegment(sketch, "E627", {"start": v(-3683, -11999.16) * mm, "end": v(-3683, -11491.16) * mm});
            skArc(sketch, "E628", {"start": v(-3683, -11491.16) * mm, "mid": v(-3720.2, -11401.36) * mm, "end": v(-3810, -11364.16) * mm});
            skLineSegment(sketch, "E629", {"start": v(-3810, -11364.16) * mm, "end": v(-4699, -11364.16) * mm});
            skArc(sketch, "E630", {"start": v(-5141.5, -775.44) * mm, "mid": v(-5204.36, -801.47) * mm, "end": v(-5230.4, -864.34) * mm});
            skLineSegment(sketch, "E631", {"start": v(-5230.4, -864.34) * mm, "end": v(-5230.4, -1372.34) * mm});
            skArc(sketch, "E632", {"start": v(-5230.4, -1372.34) * mm, "mid": v(-5204.36, -1435.2) * mm, "end": v(-5141.5, -1461.24) * mm});
            skLineSegment(sketch, "E633", {"start": v(-5141.5, -1461.24) * mm, "end": v(-4379.5, -1461.24) * mm});
            skArc(sketch, "E634", {"start": v(-4379.5, -1461.24) * mm, "mid": v(-4316.63, -1435.2) * mm, "end": v(-4290.6, -1372.34) * mm});
            skLineSegment(sketch, "E635", {"start": v(-4290.6, -1372.34) * mm, "end": v(-4290.6, -864.34) * mm});
            skArc(sketch, "E636", {"start": v(-4290.6, -864.34) * mm, "mid": v(-4316.63, -801.47) * mm, "end": v(-4379.5, -775.44) * mm});
            skLineSegment(sketch, "E637", {"start": v(-4379.5, -775.44) * mm, "end": v(-5141.5, -775.44) * mm});
            skArc(sketch, "E638", {"start": v(-5141.5, -737.34) * mm, "mid": v(-5231.3, -774.53) * mm, "end": v(-5268.5, -864.34) * mm});
            skLineSegment(sketch, "E639", {"start": v(-5268.5, -864.34) * mm, "end": v(-5268.5, -1372.34) * mm});
            skArc(sketch, "E640", {"start": v(-5268.5, -1372.34) * mm, "mid": v(-5231.3, -1462.14) * mm, "end": v(-5141.5, -1499.34) * mm});
            skLineSegment(sketch, "E641", {"start": v(-5141.5, -1499.34) * mm, "end": v(-4379.5, -1499.34) * mm});
            skArc(sketch, "E642", {"start": v(-4379.5, -1499.34) * mm, "mid": v(-4289.7, -1462.14) * mm, "end": v(-4252.5, -1372.34) * mm});
            skLineSegment(sketch, "E643", {"start": v(-4252.5, -1372.34) * mm, "end": v(-4252.5, -864.34) * mm});
            skArc(sketch, "E644", {"start": v(-4252.5, -864.34) * mm, "mid": v(-4289.7, -774.53) * mm, "end": v(-4379.5, -737.34) * mm});
            skLineSegment(sketch, "E645", {"start": v(-4379.5, -737.34) * mm, "end": v(-5141.5, -737.34) * mm});
            skArc(sketch, "E646", {"start": v(-5141.5, -1537.44) * mm, "mid": v(-5204.36, -1563.47) * mm, "end": v(-5230.4, -1626.34) * mm});
            skLineSegment(sketch, "E647", {"start": v(-5230.4, -1626.34) * mm, "end": v(-5230.4, -2134.34) * mm});
            skArc(sketch, "E648", {"start": v(-5230.4, -2134.34) * mm, "mid": v(-5204.36, -2197.2) * mm, "end": v(-5141.5, -2223.24) * mm});
            skLineSegment(sketch, "E649", {"start": v(-5141.5, -2223.24) * mm, "end": v(-4379.5, -2223.24) * mm});
            skArc(sketch, "E650", {"start": v(-4379.5, -2223.24) * mm, "mid": v(-4316.63, -2197.2) * mm, "end": v(-4290.6, -2134.34) * mm});
            skLineSegment(sketch, "E651", {"start": v(-4290.6, -2134.34) * mm, "end": v(-4290.6, -1626.34) * mm});
            skArc(sketch, "E652", {"start": v(-4290.6, -1626.34) * mm, "mid": v(-4316.63, -1563.47) * mm, "end": v(-4379.5, -1537.44) * mm});
            skLineSegment(sketch, "E653", {"start": v(-4379.5, -1537.44) * mm, "end": v(-5141.5, -1537.44) * mm});
            skArc(sketch, "E654", {"start": v(-5141.5, -1499.34) * mm, "mid": v(-5231.3, -1536.53) * mm, "end": v(-5268.5, -1626.34) * mm});
            skLineSegment(sketch, "E655", {"start": v(-5268.5, -1626.34) * mm, "end": v(-5268.5, -2134.34) * mm});
            skArc(sketch, "E656", {"start": v(-5268.5, -2134.34) * mm, "mid": v(-5231.3, -2224.14) * mm, "end": v(-5141.5, -2261.34) * mm});
            skLineSegment(sketch, "E657", {"start": v(-5141.5, -2261.34) * mm, "end": v(-4379.5, -2261.34) * mm});
            skArc(sketch, "E658", {"start": v(-4379.5, -2261.34) * mm, "mid": v(-4289.7, -2224.14) * mm, "end": v(-4252.5, -2134.34) * mm});
            skLineSegment(sketch, "E659", {"start": v(-4252.5, -2134.34) * mm, "end": v(-4252.5, -1626.34) * mm});
            skArc(sketch, "E660", {"start": v(-4252.5, -1626.34) * mm, "mid": v(-4289.7, -1536.53) * mm, "end": v(-4379.5, -1499.34) * mm});
            skLineSegment(sketch, "E661", {"start": v(-4379.5, -1499.34) * mm, "end": v(-5141.5, -1499.34) * mm});
            skArc(sketch, "E662", {"start": v(-5141.5, 1764.56) * mm, "mid": v(-5204.36, 1738.53) * mm, "end": v(-5230.4, 1675.66) * mm});
            skLineSegment(sketch, "E663", {"start": v(-5230.4, 1675.66) * mm, "end": v(-5230.4, 1167.66) * mm});
            skArc(sketch, "E664", {"start": v(-5230.4, 1167.66) * mm, "mid": v(-5204.36, 1104.8) * mm, "end": v(-5141.5, 1078.76) * mm});
            skLineSegment(sketch, "E665", {"start": v(-5141.5, 1078.76) * mm, "end": v(-4379.5, 1078.76) * mm});
            skArc(sketch, "E666", {"start": v(-4379.5, 1078.76) * mm, "mid": v(-4316.63, 1104.8) * mm, "end": v(-4290.6, 1167.66) * mm});
            skLineSegment(sketch, "E667", {"start": v(-4290.6, 1167.66) * mm, "end": v(-4290.6, 1675.66) * mm});
            skArc(sketch, "E668", {"start": v(-4290.6, 1675.66) * mm, "mid": v(-4316.63, 1738.53) * mm, "end": v(-4379.5, 1764.56) * mm});
            skLineSegment(sketch, "E669", {"start": v(-4379.5, 1764.56) * mm, "end": v(-5141.5, 1764.56) * mm});
            skArc(sketch, "E670", {"start": v(-5141.5, 1802.66) * mm, "mid": v(-5231.3, 1765.47) * mm, "end": v(-5268.5, 1675.66) * mm});
            skLineSegment(sketch, "E671", {"start": v(-5268.5, 1675.66) * mm, "end": v(-5268.5, 1167.66) * mm});
            skArc(sketch, "E672", {"start": v(-5268.5, 1167.66) * mm, "mid": v(-5231.3, 1077.86) * mm, "end": v(-5141.5, 1040.66) * mm});
            skLineSegment(sketch, "E673", {"start": v(-5141.5, 1040.66) * mm, "end": v(-4379.5, 1040.66) * mm});
            skArc(sketch, "E674", {"start": v(-4379.5, 1040.66) * mm, "mid": v(-4289.7, 1077.86) * mm, "end": v(-4252.5, 1167.66) * mm});
            skLineSegment(sketch, "E675", {"start": v(-4252.5, 1167.66) * mm, "end": v(-4252.5, 1675.66) * mm});
            skArc(sketch, "E676", {"start": v(-4252.5, 1675.66) * mm, "mid": v(-4289.7, 1765.47) * mm, "end": v(-4379.5, 1802.66) * mm});
            skLineSegment(sketch, "E677", {"start": v(-4379.5, 1802.66) * mm, "end": v(-5141.5, 1802.66) * mm});
            skArc(sketch, "E678", {"start": v(-5141.5, 1002.56) * mm, "mid": v(-5204.36, 976.53) * mm, "end": v(-5230.4, 913.66) * mm});
            skLineSegment(sketch, "E679", {"start": v(-5230.4, 913.66) * mm, "end": v(-5230.4, 405.66) * mm});
            skArc(sketch, "E680", {"start": v(-5230.4, 405.66) * mm, "mid": v(-5204.36, 342.8) * mm, "end": v(-5141.5, 316.76) * mm});
            skLineSegment(sketch, "E681", {"start": v(-5141.5, 316.76) * mm, "end": v(-4379.5, 316.76) * mm});
            skArc(sketch, "E682", {"start": v(-4379.5, 316.76) * mm, "mid": v(-4316.63, 342.8) * mm, "end": v(-4290.6, 405.66) * mm});
            skLineSegment(sketch, "E683", {"start": v(-4290.6, 405.66) * mm, "end": v(-4290.6, 913.66) * mm});
            skArc(sketch, "E684", {"start": v(-4290.6, 913.66) * mm, "mid": v(-4316.63, 976.53) * mm, "end": v(-4379.5, 1002.56) * mm});
            skLineSegment(sketch, "E685", {"start": v(-4379.5, 1002.56) * mm, "end": v(-5141.5, 1002.56) * mm});
            skArc(sketch, "E686", {"start": v(-5141.5, 1040.66) * mm, "mid": v(-5231.3, 1003.47) * mm, "end": v(-5268.5, 913.66) * mm});
            skLineSegment(sketch, "E687", {"start": v(-5268.5, 913.66) * mm, "end": v(-5268.5, 405.66) * mm});
            skArc(sketch, "E688", {"start": v(-5268.5, 405.66) * mm, "mid": v(-5231.3, 315.86) * mm, "end": v(-5141.5, 278.66) * mm});
            skLineSegment(sketch, "E689", {"start": v(-5141.5, 278.66) * mm, "end": v(-4379.5, 278.66) * mm});
            skArc(sketch, "E690", {"start": v(-4379.5, 278.66) * mm, "mid": v(-4289.7, 315.86) * mm, "end": v(-4252.5, 405.66) * mm});
            skLineSegment(sketch, "E691", {"start": v(-4252.5, 405.66) * mm, "end": v(-4252.5, 913.66) * mm});
            skArc(sketch, "E692", {"start": v(-4252.5, 913.66) * mm, "mid": v(-4289.7, 1003.47) * mm, "end": v(-4379.5, 1040.66) * mm});
            skLineSegment(sketch, "E693", {"start": v(-4379.5, 1040.66) * mm, "end": v(-5141.5, 1040.66) * mm});
            skArc(sketch, "E694", {"start": v(-6262.6, 1510.56) * mm, "mid": v(-6325.46, 1484.53) * mm, "end": v(-6351.5, 1421.66) * mm});
            skLineSegment(sketch, "E695", {"start": v(-6351.5, 1421.66) * mm, "end": v(-6351.5, 913.66) * mm});
            skArc(sketch, "E696", {"start": v(-6351.5, 913.66) * mm, "mid": v(-6325.46, 850.8) * mm, "end": v(-6262.6, 824.76) * mm});
            skLineSegment(sketch, "E697", {"start": v(-6262.6, 824.76) * mm, "end": v(-5500.6, 824.76) * mm});
            skArc(sketch, "E698", {"start": v(-5500.6, 824.76) * mm, "mid": v(-5437.74, 850.8) * mm, "end": v(-5411.7, 913.66) * mm});
            skLineSegment(sketch, "E699", {"start": v(-5411.7, 913.66) * mm, "end": v(-5411.7, 1421.66) * mm});
            skArc(sketch, "E700", {"start": v(-5411.7, 1421.66) * mm, "mid": v(-5437.74, 1484.53) * mm, "end": v(-5500.6, 1510.56) * mm});
            skLineSegment(sketch, "E701", {"start": v(-5500.6, 1510.56) * mm, "end": v(-6262.6, 1510.56) * mm});
            skArc(sketch, "E702", {"start": v(-6262.6, 1548.66) * mm, "mid": v(-6352.4, 1511.47) * mm, "end": v(-6389.6, 1421.66) * mm});
            skLineSegment(sketch, "E703", {"start": v(-6389.6, 1421.66) * mm, "end": v(-6389.6, 913.66) * mm});
            skArc(sketch, "E704", {"start": v(-6389.6, 913.66) * mm, "mid": v(-6352.4, 823.86) * mm, "end": v(-6262.6, 786.66) * mm});
            skLineSegment(sketch, "E705", {"start": v(-6262.6, 786.66) * mm, "end": v(-5500.6, 786.66) * mm});
            skArc(sketch, "E706", {"start": v(-5500.6, 786.66) * mm, "mid": v(-5410.8, 823.86) * mm, "end": v(-5373.6, 913.66) * mm});
            skLineSegment(sketch, "E707", {"start": v(-5373.6, 913.66) * mm, "end": v(-5373.6, 1421.66) * mm});
            skArc(sketch, "E708", {"start": v(-5373.6, 1421.66) * mm, "mid": v(-5410.8, 1511.47) * mm, "end": v(-5500.6, 1548.66) * mm});
            skLineSegment(sketch, "E709", {"start": v(-5500.6, 1548.66) * mm, "end": v(-6262.6, 1548.66) * mm});
            skArc(sketch, "E710", {"start": v(10147.3, 6797.67) * mm, "mid": v(10084.44, 6771.64) * mm, "end": v(10058.4, 6708.78) * mm});
            skLineSegment(sketch, "E711", {"start": v(10058.4, 6708.78) * mm, "end": v(10058.4, 5991.23) * mm});
            skArc(sketch, "E712", {"start": v(10058.4, 5991.23) * mm, "mid": v(10084.44, 5928.36) * mm, "end": v(10147.3, 5902.33) * mm});
            skLineSegment(sketch, "E713", {"start": v(10147.3, 5902.32) * mm, "end": v(11188.7, 5902.32) * mm});
            skArc(sketch, "E714", {"start": v(11188.7, 5902.33) * mm, "mid": v(11251.56, 5928.36) * mm, "end": v(11277.6, 5991.23) * mm});
            skLineSegment(sketch, "E715", {"start": v(11277.6, 5991.23) * mm, "end": v(11277.6, 6708.78) * mm});
            skArc(sketch, "E716", {"start": v(11277.6, 6708.78) * mm, "mid": v(11251.56, 6771.64) * mm, "end": v(11188.7, 6797.67) * mm});
            skLineSegment(sketch, "E717", {"start": v(11188.7, 6797.68) * mm, "end": v(10147.3, 6797.68) * mm});
            skArc(sketch, "E718", {"start": v(10147.3, 6835.77) * mm, "mid": v(10057.5, 6798.58) * mm, "end": v(10020.3, 6708.78) * mm});
            skLineSegment(sketch, "E719", {"start": v(10020.3, 6708.78) * mm, "end": v(10020.3, 5991.23) * mm});
            skArc(sketch, "E720", {"start": v(10020.3, 5991.23) * mm, "mid": v(10057.5, 5901.42) * mm, "end": v(10147.3, 5864.23) * mm});
            skLineSegment(sketch, "E721", {"start": v(10147.3, 5864.23) * mm, "end": v(11188.7, 5864.23) * mm});
            skArc(sketch, "E722", {"start": v(11188.7, 5864.23) * mm, "mid": v(11278.5, 5901.42) * mm, "end": v(11315.7, 5991.23) * mm});
            skLineSegment(sketch, "E723", {"start": v(11315.7, 5991.23) * mm, "end": v(11315.7, 6708.78) * mm});
            skArc(sketch, "E724", {"start": v(11315.7, 6708.78) * mm, "mid": v(11278.5, 6798.58) * mm, "end": v(11188.7, 6835.77) * mm});
            skLineSegment(sketch, "E725", {"start": v(11188.7, 6835.78) * mm, "end": v(10147.3, 6835.78) * mm});
            skLineSegment(sketch, "E726", {"start": v(455.7, 2590.57) * mm, "end": v(509.98, 2644.85) * mm});
            skLineSegment(sketch, "E727", {"start": v(509.98, 2644.85) * mm, "end": v(19.7, 3135.13) * mm});
            skLineSegment(sketch, "E728", {"start": v(19.7, 3135.13) * mm, "end": v(-34.57, 3080.85) * mm});
            skLineSegment(sketch, "E729", {"start": v(-34.57, 3080.85) * mm, "end": v(455.7, 2590.57) * mm});
            skLineSegment(sketch, "E730", {"start": v(-57.74, 3048.94) * mm, "end": v(51.46, 3158.14) * mm});
            skLineSegment(sketch, "E731", {"start": v(51.46, 3158.14) * mm, "end": v(-17.8, 3227.4) * mm});
            skLineSegment(sketch, "E732", {"start": v(-17.8, 3227.4) * mm, "end": v(-127, 3118.2) * mm});
            skLineSegment(sketch, "E733", {"start": v(-127, 3118.2) * mm, "end": v(-57.74, 3048.94) * mm});
            skLineSegment(sketch, "E734", {"start": v(51.19, 3157.6) * mm, "end": v(106.68, 3282.95) * mm});
            skLineSegment(sketch, "E735", {"start": v(106.68, 3282.95) * mm, "end": v(-18.66, 3227.46) * mm});
            skLineSegment(sketch, "E736", {"start": v(-18.66, 3227.46) * mm, "end": v(51.19, 3157.6) * mm});
            skEllipticalArc(sketch, "E737", {});
            skEllipticalArc(sketch, "E738", {});
            skArc(sketch, "E739", {"start": v(-10951.22, -10234.88) * mm, "mid": v(-11359.64, -10541.45) * mm, "end": v(-11558.56, -11011.8) * mm});
            skArc(sketch, "E740", {"start": v(-10783.13, -10184.55) * mm, "mid": v(-10868.3, -10205.95) * mm, "end": v(-10951.22, -10234.88) * mm});
            skArc(sketch, "E741", {"start": v(-10783.13, -10184.55) * mm, "mid": v(-10880.7, -10169.7) * mm, "end": v(-10979.28, -10164.73) * mm});
            skArc(sketch, "E742", {"start": v(-10979.28, -10164.73) * mm, "mid": v(-11960, -11145.45) * mm, "end": v(-10979.28, -12126.16) * mm});
            skArc(sketch, "E743", {"start": v(-10979.28, -12126.16) * mm, "mid": v(-10880.7, -12121.2) * mm, "end": v(-10783.13, -12106.35) * mm});
            skArc(sketch, "E744", {"start": v(-10951.22, -12056.02) * mm, "mid": v(-10868.3, -12084.95) * mm, "end": v(-10783.13, -12106.35) * mm});
            skArc(sketch, "E745", {"start": v(-11564.38, -11226.11) * mm, "mid": v(-11375.77, -11728.22) * mm, "end": v(-10951.22, -12056.02) * mm});
            skEllipticalArc(sketch, "E746", {});
            const initialGuessF0  = {"E56": [-0.2869538838000012, -8.290803255800002, 0, -16.409576, 0.41680323040000006, 0.3187319254, -4.712389, -1.570796], "E57": [-0.2869538838000012, -8.290803255800002, 0, -16.409576, 0.41680323040000006, 0.3187319254, -1.570796, -0.36375], "E65": [-0.2869538838000012, -8.290803255800002, 0, -16.409576, 0.41680323040000006, 0.3187319254, 0.322176, 1.570796], "E66": [-0.2996538838000012, 1.8069667442000015, 0, -16.409576, 0.41680323040000006, 0.3187319254, -4.712389, -1.570796], "E67": [-0.2996538838000012, 1.8069667442000015, 0, -16.409576, 0.41680323040000006, 0.3187319254, -1.570796, -0.36375], "E75": [-0.2996538838000012, 1.8069667442000015, 0, -16.409576, 0.41680323040000006, 0.3187319254, 0.322176, 1.570796], "E76": [5.9868461162, 4.836986236600001, 0, -16.409576, 0.41680323040000006, 0.3187319254, -4.712389, -1.570796], "E77": [5.9868461162, 4.836986236600001, 0, -16.409576, 0.41680323040000006, 0.3187319254, -1.570796, -0.36375], "E85": [5.9868461162, 4.836986236600001, 0, -16.409576, 0.41680323040000006, 0.3187319254, 0.322176, 1.570796], "E249": [10.570392245000003, 9.182207061000002, 0, 112.556277, 2.8589294358, 2.4239261656, 5.964552, 6.202561], "E253": [10.765607755000003, 9.182207061000002, 0, 112.556277, 2.8589294358, 2.4239261656, 0.080624, 0.318633], "E312": [-9.9014363058, -1.496260533, 0, -10.054058, 0.2553730732, 0.11561376420000001, 0, 3.141593], "E313": [-9.9014363058, -1.496260533, 0, -10.054058, 0.2553730732, 0.11561376420000001, -3.141593, 0], "E346": [-7.948847805600002, -1.496260533, 0, -90.79119, 2.306096226, 1.9140506296000002, -1.920141, -1.221452], "E351": [-9.458941559600001, -11.256210533, 0, -10.054058, 0.2553730732, 0.11561376420000001, 0, 3.141593], "E352": [-9.458941559600001, -11.256210533, 0, -10.054058, 0.2553730732, 0.11561376420000001, -3.141593, 0], "E385": [-7.506353059400001, -11.256210533, 0, -90.79119, 2.306096226, 1.9140506296000002, -1.920141, -1.221452], "E737": [-11.169024296400002, -11.1251931674, -16.409576, 0, 0.41680323040000006, 0.3187319254, -4.712389, -1.570796], "E738": [-11.169024296400002, -11.1251931674, -16.409576, 0, 0.41680323040000006, 0.3187319254, -1.570796, -0.36375], "E746": [-11.169024296400002, -11.1251931674, -16.409576, 0, 0.41680323040000006, 0.3187319254, 0.322176, 1.570796]};
            skSetInitialGuess(sketch, initialGuessF0);
            skSolve(sketch);
        }
        {
            var Q0;
            {var subQ1=sQuery(id+"F0.wireOp",EDGE,"E24");Q0=makeQuery(id+"F0.imprint","IMPRINT",FACE,{"disambiguationData":[TD([[makeQuery(id+"F0.imprint","IMPRINT",EDGE,{"derivedFrom":subQ1}),1.0]])]});}
            var Q1;
            Q1=makeQuery(id+"F0.imprint","IMPRINT",FACE,{"disambiguationData":[TD([[makeQuery(id+"F0.imprint","IMPRINT",EDGE,{"derivedFrom":sQuery(id+"F0.wireOp",EDGE,"E438")}),1.0]])]});
            var Q2;
            Q2=makeQuery(id+"F0.imprint","IMPRINT",FACE,{"disambiguationData":[TD([[makeQuery(id+"F0.imprint","IMPRINT",EDGE,{"derivedFrom":sQuery(id+"F0.wireOp",EDGE,"E422")}),1.0]])]});
            var Q3;
            Q3=makeQuery(id+"F0.imprint","IMPRINT",FACE,{"disambiguationData":[TD([[makeQuery(id+"F0.imprint","IMPRINT",EDGE,{"derivedFrom":sQuery(id+"F0.wireOp",EDGE,"E406")}),1.0]])]});
            var Q4;
            Q4=makeQuery(id+"F0.imprint","IMPRINT",FACE,{"disambiguationData":[TD([[makeQuery(id+"F0.imprint","IMPRINT",EDGE,{"derivedFrom":sQuery(id+"F0.wireOp",EDGE,"E390")}),1.0]])]});
            var Q5;
            {var subQ7=sQuery(id+"F0.wireOp",EDGE,"E48");Q5=makeQuery(id+"F0.imprint","IMPRINT",FACE,{"disambiguationData":[TD([[makeQuery(id+"F0.imprint","IMPRINT",EDGE,{"derivedFrom":subQ7}),1.0]])]});}
            var Q6;
            Q6=makeQuery(id+"F0.imprint","IMPRINT",FACE,{"disambiguationData":[TD([[makeQuery(id+"F0.imprint","IMPRINT",EDGE,{"derivedFrom":sQuery(id+"F0.wireOp",EDGE,"E454")}),1.0]])]});
            var Q7;
            Q7=makeQuery(id+"F0.imprint","IMPRINT",FACE,{"disambiguationData":[TD([[makeQuery(id+"F0.imprint","IMPRINT",EDGE,{"derivedFrom":sQuery(id+"F0.wireOp",EDGE,"E470")}),1.0]])]});
            var Q8;
            Q8=makeQuery(id+"F0.imprint","IMPRINT",FACE,{"disambiguationData":[TD([[makeQuery(id+"F0.imprint","IMPRINT",EDGE,{"derivedFrom":sQuery(id+"F0.wireOp",EDGE,"E486")}),1.0]])]});
            var Q9;
            Q9=makeQuery(id+"F0.imprint","IMPRINT",FACE,{"disambiguationData":[TD([[makeQuery(id+"F0.imprint","IMPRINT",EDGE,{"derivedFrom":sQuery(id+"F0.wireOp",EDGE,"E502")}),1.0]])]});
            var Q10;
            Q10=makeQuery(id+"F0.imprint","IMPRINT",FACE,{"disambiguationData":[TD([[makeQuery(id+"F0.imprint","IMPRINT",EDGE,{"derivedFrom":sQuery(id+"F0.wireOp",EDGE,"E518")}),1.0]])]});
            var Q11;
            {var subQ1=sQuery(id+"F0.wireOp",EDGE,"E53");Q11=makeQuery(id+"F0.imprint","IMPRINT",FACE,{"disambiguationData":[TD([[makeQuery(id+"F0.imprint","IMPRINT",EDGE,{"derivedFrom":subQ1}),1.0]])]});}
            var Q12;
            Q12=makeQuery(id+"F0.imprint","IMPRINT",FACE,{"disambiguationData":[TD([[makeQuery(id+"F0.imprint","IMPRINT",EDGE,{"derivedFrom":sQuery(id+"F0.wireOp",EDGE,"E534")}),1.0]])]});
            extrude(context, id + "F1", {"entities" : qUnion([Q0, Q1, Q2, Q3, Q4, Q5, Q6, Q7, Q8, Q9, Q10, Q11, Q12]), "depth" : 1000 * mm});
        }
        {
            var Q0;
            Q0=makeQuery(id+"F1.opExtrude","CAP_FACE",FACE,{"disambiguationData":[OSD([sQuery(id+"F0.wireOp",EDGE,"E390"),sQuery(id+"F0.wireOp",EDGE,"E391"),sQuery(id+"F0.wireOp",EDGE,"E392"),sQuery(id+"F0.wireOp",EDGE,"E393"),sQuery(id+"F0.wireOp",EDGE,"E394"),sQuery(id+"F0.wireOp",EDGE,"E395"),sQuery(id+"F0.wireOp",EDGE,"E396"),sQuery(id+"F0.wireOp",EDGE,"E397")])],"isStart":false});
            var Q1;
            Q1=makeQuery(id+"F1.opExtrude","CAP_FACE",FACE,{"disambiguationData":[OSD([sQuery(id+"F0.wireOp",EDGE,"E406"),sQuery(id+"F0.wireOp",EDGE,"E407"),sQuery(id+"F0.wireOp",EDGE,"E408"),sQuery(id+"F0.wireOp",EDGE,"E409"),sQuery(id+"F0.wireOp",EDGE,"E410"),sQuery(id+"F0.wireOp",EDGE,"E411"),sQuery(id+"F0.wireOp",EDGE,"E412"),sQuery(id+"F0.wireOp",EDGE,"E413")])],"isStart":false});
            var Q2;
            Q2=makeQuery(id+"F1.opExtrude","CAP_FACE",FACE,{"disambiguationData":[OSD([sQuery(id+"F0.wireOp",EDGE,"E422"),sQuery(id+"F0.wireOp",EDGE,"E423"),sQuery(id+"F0.wireOp",EDGE,"E424"),sQuery(id+"F0.wireOp",EDGE,"E425"),sQuery(id+"F0.wireOp",EDGE,"E426"),sQuery(id+"F0.wireOp",EDGE,"E427"),sQuery(id+"F0.wireOp",EDGE,"E428"),sQuery(id+"F0.wireOp",EDGE,"E429")])],"isStart":false});
            var Q3;
            Q3=makeQuery(id+"F1.opExtrude","CAP_FACE",FACE,{"disambiguationData":[OSD([sQuery(id+"F0.wireOp",EDGE,"E438"),sQuery(id+"F0.wireOp",EDGE,"E439"),sQuery(id+"F0.wireOp",EDGE,"E440"),sQuery(id+"F0.wireOp",EDGE,"E441"),sQuery(id+"F0.wireOp",EDGE,"E442"),sQuery(id+"F0.wireOp",EDGE,"E443"),sQuery(id+"F0.wireOp",EDGE,"E444"),sQuery(id+"F0.wireOp",EDGE,"E445")])],"isStart":false});
            var Q4;
            Q4=makeQuery(id+"F1.opExtrude","CAP_FACE",FACE,{"disambiguationData":[OSD([sQuery(id+"F0.wireOp",EDGE,"E454"),sQuery(id+"F0.wireOp",EDGE,"E455"),sQuery(id+"F0.wireOp",EDGE,"E456"),sQuery(id+"F0.wireOp",EDGE,"E457"),sQuery(id+"F0.wireOp",EDGE,"E458"),sQuery(id+"F0.wireOp",EDGE,"E459"),sQuery(id+"F0.wireOp",EDGE,"E460"),sQuery(id+"F0.wireOp",EDGE,"E461")])],"isStart":false});
            var Q5;
            Q5=makeQuery(id+"F1.opExtrude","CAP_FACE",FACE,{"disambiguationData":[OSD([sQuery(id+"F0.wireOp",EDGE,"E470"),sQuery(id+"F0.wireOp",EDGE,"E471"),sQuery(id+"F0.wireOp",EDGE,"E472"),sQuery(id+"F0.wireOp",EDGE,"E473"),sQuery(id+"F0.wireOp",EDGE,"E474"),sQuery(id+"F0.wireOp",EDGE,"E475"),sQuery(id+"F0.wireOp",EDGE,"E476"),sQuery(id+"F0.wireOp",EDGE,"E477")])],"isStart":false});
            var Q6;
            Q6=makeQuery(id+"F1.opExtrude","CAP_FACE",FACE,{"disambiguationData":[OSD([sQuery(id+"F0.wireOp",EDGE,"E486"),sQuery(id+"F0.wireOp",EDGE,"E487"),sQuery(id+"F0.wireOp",EDGE,"E488"),sQuery(id+"F0.wireOp",EDGE,"E489"),sQuery(id+"F0.wireOp",EDGE,"E490"),sQuery(id+"F0.wireOp",EDGE,"E491"),sQuery(id+"F0.wireOp",EDGE,"E492"),sQuery(id+"F0.wireOp",EDGE,"E493")])],"isStart":false});
            var Q7;
            Q7=makeQuery(id+"F1.opExtrude","CAP_FACE",FACE,{"disambiguationData":[OSD([sQuery(id+"F0.wireOp",EDGE,"E502"),sQuery(id+"F0.wireOp",EDGE,"E503"),sQuery(id+"F0.wireOp",EDGE,"E504"),sQuery(id+"F0.wireOp",EDGE,"E505"),sQuery(id+"F0.wireOp",EDGE,"E506"),sQuery(id+"F0.wireOp",EDGE,"E507"),sQuery(id+"F0.wireOp",EDGE,"E508"),sQuery(id+"F0.wireOp",EDGE,"E509")])],"isStart":false});
            var Q8;
            Q8=makeQuery(id+"F1.opExtrude","CAP_FACE",FACE,{"disambiguationData":[OSD([sQuery(id+"F0.wireOp",EDGE,"E518"),sQuery(id+"F0.wireOp",EDGE,"E519"),sQuery(id+"F0.wireOp",EDGE,"E520"),sQuery(id+"F0.wireOp",EDGE,"E521"),sQuery(id+"F0.wireOp",EDGE,"E522"),sQuery(id+"F0.wireOp",EDGE,"E523"),sQuery(id+"F0.wireOp",EDGE,"E524"),sQuery(id+"F0.wireOp",EDGE,"E525")])],"isStart":false});
            var Q9;
            Q9=makeQuery(id+"F1.opExtrude","CAP_FACE",FACE,{"disambiguationData":[OSD([sQuery(id+"F0.wireOp",EDGE,"E534"),sQuery(id+"F0.wireOp",EDGE,"E535"),sQuery(id+"F0.wireOp",EDGE,"E536"),sQuery(id+"F0.wireOp",EDGE,"E537"),sQuery(id+"F0.wireOp",EDGE,"E538"),sQuery(id+"F0.wireOp",EDGE,"E539"),sQuery(id+"F0.wireOp",EDGE,"E540"),sQuery(id+"F0.wireOp",EDGE,"E541")])],"isStart":false});
            extrude(context, id + "F2", {"entities" : qUnion([Q0, Q1, Q2, Q3, Q4, Q5, Q6, Q7, Q8, Q9]), "depth" : 300 * mm});
        }
    });
